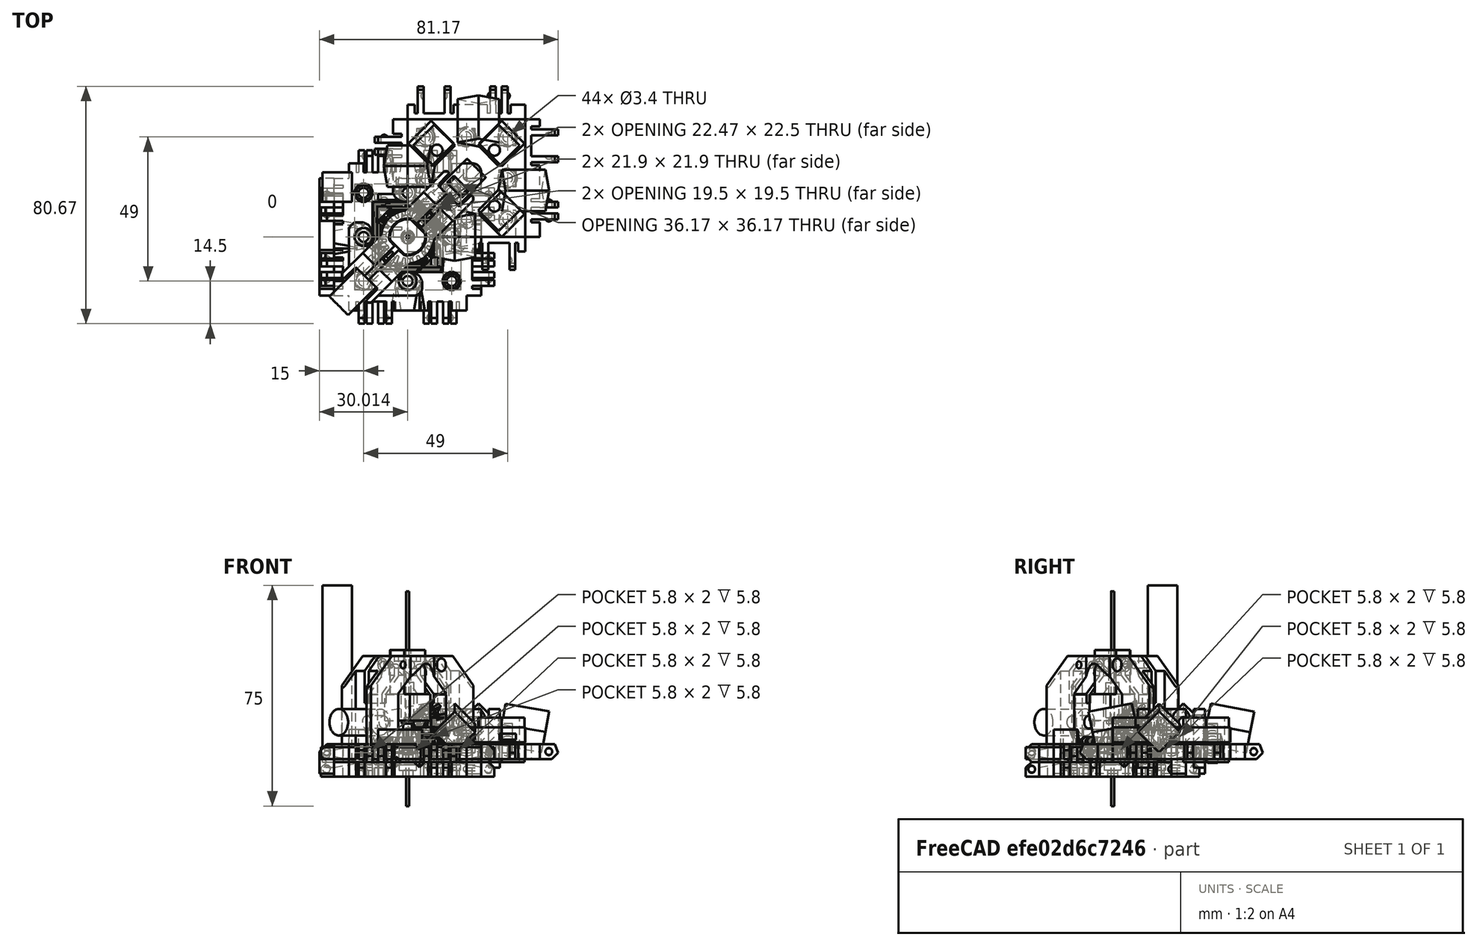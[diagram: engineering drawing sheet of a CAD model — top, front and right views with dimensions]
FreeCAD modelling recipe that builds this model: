
FCSTD DOCUMENT  (FreeCAD 0.18R16146 (Git))
Label: Robot 0.2
License: All rights reserved
LicenseURL: http://en.wikipedia.org/wiki/All_rights_reserved
objects: Part::Box×352, Part::Cut×133, Part::Sphere×107, Part::MultiFuse×99, Part::Cylinder×68, Part::Fuse×45, Part::Chamfer×23, Part::Feature×21, Drawing::FeatureViewAnnotation×10, Part::Fillet×7, App::DocumentObjectGroup×4, Part::MultiCommon×4, Drawing::FeaturePage×2, Part::FeaturePython×2, Part::Cone×2, Part::Mirroring×1
note: 864 computed .brp shape members not serialized (recipe doc carries the construction recipe); baked Part::Feature solids carry a one-line shape summary decoded from their .brp

FEATURE [Part::Box] Box  label="Cube"
  AttacherType = Attacher::AttachEngine3D
  Height = 5
  Length = 40
  Placement = pos=(-20,-20,-2) rot=(0,0,1;0rad)
  Width = 40
FEATURE [Part::Sphere] Sphere003  label="Mag Hole 3"
  Angle1 = -90
  Angle2 = 90
  Angle3 = 360
  AttacherType = Attacher::AttachEngine3D
  Placement = pos=(-15,15,1.7) rot=(0,0,1;0rad)
  Radius = 2.83
FEATURE [Part::Sphere] Sphere005  label="Mag Hole 2"
  Angle1 = -90
  Angle2 = 90
  Angle3 = 360
  AttacherType = Attacher::AttachEngine3D
  Placement = pos=(15,0,1.7) rot=(0,0,1;0rad)
  Radius = 2.825
FEATURE [Part::Sphere] Sphere  label="Mag Hole"
  Angle1 = -90
  Angle2 = 90
  Angle3 = 360
  AttacherType = Attacher::AttachEngine3D
  Placement = pos=(-15,-15,1.7) rot=(0,0,1;0rad)
  Radius = 2.83
FEATURE [Part::MultiFuse] Fusion004  label="Ball Holes"
  Shapes = -> [Sphere,Sphere005,Sphere003]
FEATURE [Part::Cut] Cut003
  Base = -> Box
  Tool = -> Fusion004
FEATURE [Part::Box] Box001  label="Cube001"
  AttacherType = Attacher::AttachEngine3D
  Height = 7
  Length = 5
  Placement = pos=(-5,0,-2) rot=(0,0,1;0rad)
  Width = 40
FEATURE [Part::Box] Box002  label="Cube002"
  AttacherType = Attacher::AttachEngine3D
  Height = 7
  Length = 10
  Placement = pos=(-15,6,-2) rot=(0,0,1;0rad)
  Width = 2
FEATURE [Part::Box] Box003  label="Cube003"
  AttacherType = Attacher::AttachEngine3D
  Height = 7
  Length = 10
  Placement = pos=(-15,10,-2) rot=(0,0,1;0rad)
  Width = 2
FEATURE [Part::Box] Box004  label="Cube004"
  AttacherType = Attacher::AttachEngine3D
  Height = 7
  Length = 10
  Placement = pos=(-15,25.4,-2) rot=(0,0,1;0rad)
  Width = 2
FEATURE [Part::Box] Box005  label="Cube005"
  AttacherType = Attacher::AttachEngine3D
  Height = 7
  Length = 10
  Placement = pos=(-15,34.6,-2) rot=(0,0,1;0rad)
  Width = 2
FEATURE [Part::Sphere] Sphere008
  Angle1 = -90
  Angle2 = 90
  Angle3 = 360
  AttacherType = Attacher::AttachEngine3D
  Placement = pos=(-7.5,6.5,0.5) rot=(0,0,1;0rad)
  Radius = 1.25
FEATURE [Part::Box] Box006  label="Chamfer Cube"
  AttacherType = Attacher::AttachEngine3D
  Height = 10
  Length = 13
  Placement = pos=(-11.69,0,-1.19) rot=(0,-1,0;0.785398rad)
  Width = 40
FEATURE [Part::Sphere] Sphere009
  Angle1 = -90
  Angle2 = 90
  Angle3 = 360
  AttacherType = Attacher::AttachEngine3D
  Placement = pos=(-7.5,11.5,0.5) rot=(0,0,1;0rad)
  Radius = 1.25
FEATURE [Part::Sphere] Sphere010
  Angle1 = -90
  Angle2 = 90
  Angle3 = 360
  AttacherType = Attacher::AttachEngine3D
  Placement = pos=(-7.5,28,0.5) rot=(0,0,1;0rad)
  Radius = 1.5
FEATURE [Part::Sphere] Sphere011
  Angle1 = -90
  Angle2 = 90
  Angle3 = 360
  AttacherType = Attacher::AttachEngine3D
  Placement = pos=(-7.5,34,0.5) rot=(0,0,1;0rad)
  Radius = 1.5
FEATURE [Part::Box] Box007  label="Cube007"
  AttacherType = Attacher::AttachEngine3D
  Height = 7
  Length = 4
  Placement = pos=(-6,5,-2) rot=(0,0,1;0rad)
  Width = 1
FEATURE [Part::Box] Box008  label="Cube008"
  AttacherType = Attacher::AttachEngine3D
  Height = 7
  Length = 4
  Placement = pos=(-6,8,-2) rot=(0,0,1;0rad)
  Width = 2
FEATURE [Part::Box] Box009  label="Cube009"
  AttacherType = Attacher::AttachEngine3D
  Height = 7
  Length = 4
  Placement = pos=(-6,12,-2) rot=(0,0,1;0rad)
  Width = 1
FEATURE [Part::Box] Box010  label="Cube010"
  AttacherType = Attacher::AttachEngine3D
  Height = 7
  Length = 4
  Placement = pos=(-6,24.4,-2) rot=(0,0,1;0rad)
  Width = 1
FEATURE [Part::Box] Box011  label="Cube011"
  AttacherType = Attacher::AttachEngine3D
  Height = 7
  Length = 4
  Placement = pos=(-6,36.6,-2) rot=(0,0,1;0rad)
  Width = 1
FEATURE [Part::Box] Box012  label="Cube012"
  AttacherType = Attacher::AttachEngine3D
  Height = 7
  Length = 4
  Placement = pos=(-6,27.4,-2) rot=(0,0,1;0rad)
  Width = 7.2
FEATURE [Part::MultiFuse] Fusion003  label="Extra Holes for Clips"
  Shapes = -> [Box012,Box009,Box011,Box008,Box010,Box007]
FEATURE [Part::Box] Box013  label="Re-level Edge Clip Block"
  AttacherType = Attacher::AttachEngine3D
  Height = 10
  Length = 20
  Placement = pos=(-19,-2,3) rot=(0,0,1;0rad)
  Width = 44
FEATURE [Part::Box] Box014  label="Cube014"
  AttacherType = Attacher::AttachEngine3D
  Height = 7
  Length = 10
  Placement = pos=(-10,34.6,0) rot=(0,0,1;0rad)
  Width = 2
FEATURE [Part::Box] Box015  label="Cube015"
  AttacherType = Attacher::AttachEngine3D
  Height = 7
  Length = 5
  Width = 40
FEATURE [Part::Box] Box016  label="Cube016"
  AttacherType = Attacher::AttachEngine3D
  Height = 7
  Length = 10
  Placement = pos=(-10,25.4,0) rot=(0,0,1;0rad)
  Width = 2
FEATURE [Part::Box] Box017  label="Cube017"
  AttacherType = Attacher::AttachEngine3D
  Height = 7
  Length = 10
  Placement = pos=(-10,10,0) rot=(0,0,1;0rad)
  Width = 2
FEATURE [Part::Box] Box018  label="Cube018"
  AttacherType = Attacher::AttachEngine3D
  Height = 7
  Length = 10
  Placement = pos=(-10,6,0) rot=(0,0,1;0rad)
  Width = 2
FEATURE [Part::Sphere] Sphere012
  Angle1 = -90
  Angle2 = 90
  Angle3 = 360
  AttacherType = Attacher::AttachEngine3D
  Placement = pos=(-3,6.5,2.5) rot=(0,0,1;0rad)
  Radius = 1.25
FEATURE [Part::Box] Box019  label="Cube019"
  AttacherType = Attacher::AttachEngine3D
  Height = 10
  Length = 13
  Placement = pos=(-10.19,0,-1.19) rot=(0,-1,0;0.785398rad)
  Width = 40
FEATURE [Part::Sphere] Sphere013
  Angle1 = -90
  Angle2 = 90
  Angle3 = 360
  AttacherType = Attacher::AttachEngine3D
  Placement = pos=(-3,11.5,2.5) rot=(0,0,1;0rad)
  Radius = 1.25
FEATURE [Part::Sphere] Sphere014
  Angle1 = -90
  Angle2 = 90
  Angle3 = 360
  AttacherType = Attacher::AttachEngine3D
  Placement = pos=(-3,28,2.5) rot=(0,0,1;0rad)
  Radius = 1.5
FEATURE [Part::Sphere] Sphere015
  Angle1 = -90
  Angle2 = 90
  Angle3 = 360
  AttacherType = Attacher::AttachEngine3D
  Placement = pos=(-3,34,2.5) rot=(0,0,1;0rad)
  Radius = 1.5
FEATURE [Part::MultiFuse] Fusion005
  Shapes = -> [Box015,Box018,Box017,Box016,Box014]
FEATURE [Part::Cut] Cut005
  Base = -> Fusion005
  Tool = -> Box019
FEATURE [Part::MultiFuse] Fusion006
  Shapes = -> [Sphere012,Sphere013,Cut005]
FEATURE [Part::MultiFuse] Fusion007
  Shapes = -> [Sphere015,Sphere014]
FEATURE [Part::Cut] Cut006
  Base = -> Fusion006
  Tool = -> Fusion007
FEATURE [Part::Chamfer] Chamfer002
  Base = -> Cut006
  Edges = 4 edges r=4: [Edge31,Edge37,Edge43,Edge46]
FEATURE [Part::Box] Box020  label="Cube020"
  AttacherType = Attacher::AttachEngine3D
  Height = 7
  Length = 4
  Placement = pos=(-1,5,0) rot=(0,0,1;0rad)
  Width = 1
FEATURE [Part::Box] Box021  label="Cube021"
  AttacherType = Attacher::AttachEngine3D
  Height = 7
  Length = 4
  Placement = pos=(-1,8,0) rot=(0,0,1;0rad)
  Width = 2
FEATURE [Part::Box] Box022  label="Cube022"
  AttacherType = Attacher::AttachEngine3D
  Height = 7
  Length = 4
  Placement = pos=(-1,12,0) rot=(0,0,1;0rad)
  Width = 1
FEATURE [Part::Box] Box023  label="Cube023"
  AttacherType = Attacher::AttachEngine3D
  Height = 7
  Length = 4
  Placement = pos=(-1,24.4,0) rot=(0,0,1;0rad)
  Width = 1
FEATURE [Part::Box] Box024  label="Cube024"
  AttacherType = Attacher::AttachEngine3D
  Height = 7
  Length = 4
  Placement = pos=(-1,36.6,0) rot=(0,0,1;0rad)
  Width = 1
FEATURE [Part::Box] Box025  label="Cube025"
  AttacherType = Attacher::AttachEngine3D
  Height = 7
  Length = 4
  Placement = pos=(-1,27.4,0) rot=(0,0,1;0rad)
  Width = 7.2
FEATURE [Part::MultiFuse] Fusion008
  Shapes = -> [Box025,Box022,Box024,Box021,Box023,Box020]
FEATURE [Part::Cut] Cut007
  Base = -> Chamfer002
  Placement = pos=(-5,40,3) rot=(1,0,0;3.14159rad)
  Tool = -> Fusion008
FEATURE [Part::Box] Box026  label="Cube026"
  AttacherType = Attacher::AttachEngine3D
  Height = 10
  Length = 12
  Placement = pos=(-11,-2,-12) rot=(0,0,1;0rad)
  Width = 44
FEATURE [Part::Cut] Cut008
  Base = -> Cut007
  Placement = pos=(40,0,0) rot=(0,0,1;1.5708rad)
  Tool = -> Box026
FEATURE [Part::Box] Box027  label="Cube027"
  AttacherType = Attacher::AttachEngine3D
  Height = 7
  Length = 4
  Placement = pos=(-1,12,0) rot=(0,0,1;0rad)
  Width = 1
FEATURE [Part::Box] Box028  label="Cube028"
  AttacherType = Attacher::AttachEngine3D
  Height = 10
  Length = 13
  Placement = pos=(-10.19,0,-1.19) rot=(0,-1,0;0.785398rad)
  Width = 40
FEATURE [Part::Box] Box029  label="Cube029"
  AttacherType = Attacher::AttachEngine3D
  Height = 7
  Length = 4
  Placement = pos=(-1,27.4,0) rot=(0,0,1;0rad)
  Width = 7.2
FEATURE [Part::Box] Box030  label="Cube030"
  AttacherType = Attacher::AttachEngine3D
  Height = 7
  Length = 4
  Placement = pos=(-1,5,0) rot=(0,0,1;0rad)
  Width = 1
FEATURE [Part::Box] Box031  label="Cube031"
  AttacherType = Attacher::AttachEngine3D
  Height = 7
  Length = 10
  Placement = pos=(-10,6,0) rot=(0,0,1;0rad)
  Width = 2
FEATURE [Part::Box] Box032  label="Cube032"
  AttacherType = Attacher::AttachEngine3D
  Height = 10
  Length = 12
  Placement = pos=(-11,-2,-12) rot=(0,0,1;0rad)
  Width = 44
FEATURE [Part::Sphere] Sphere016
  Angle1 = -90
  Angle2 = 90
  Angle3 = 360
  AttacherType = Attacher::AttachEngine3D
  Placement = pos=(-3,6.5,2.5) rot=(0,0,1;0rad)
  Radius = 1.25
FEATURE [Part::Box] Box033  label="Cube033"
  AttacherType = Attacher::AttachEngine3D
  Height = 7
  Length = 10
  Placement = pos=(-10,25.4,0) rot=(0,0,1;0rad)
  Width = 2
FEATURE [Part::Box] Box034  label="Cube034"
  AttacherType = Attacher::AttachEngine3D
  Height = 7
  Length = 10
  Placement = pos=(-10,10,0) rot=(0,0,1;0rad)
  Width = 2
FEATURE [Part::Sphere] Sphere017
  Angle1 = -90
  Angle2 = 90
  Angle3 = 360
  AttacherType = Attacher::AttachEngine3D
  Placement = pos=(-3,28,2.5) rot=(0,0,1;0rad)
  Radius = 1.5
FEATURE [Part::Sphere] Sphere018
  Angle1 = -90
  Angle2 = 90
  Angle3 = 360
  AttacherType = Attacher::AttachEngine3D
  Placement = pos=(-3,11.5,2.5) rot=(0,0,1;0rad)
  Radius = 1.25
FEATURE [Part::Box] Box035  label="Cube035"
  AttacherType = Attacher::AttachEngine3D
  Height = 7
  Length = 4
  Placement = pos=(-1,36.6,0) rot=(0,0,1;0rad)
  Width = 1
FEATURE [Part::Sphere] Sphere019
  Angle1 = -90
  Angle2 = 90
  Angle3 = 360
  AttacherType = Attacher::AttachEngine3D
  Placement = pos=(-3,34,2.5) rot=(0,0,1;0rad)
  Radius = 1.5
FEATURE [Part::MultiFuse] Fusion011
  Shapes = -> [Sphere019,Sphere017]
FEATURE [Part::Box] Box036  label="Cube036"
  AttacherType = Attacher::AttachEngine3D
  Height = 7
  Length = 4
  Placement = pos=(-1,8,0) rot=(0,0,1;0rad)
  Width = 2
FEATURE [Part::Box] Box037  label="Cube037"
  AttacherType = Attacher::AttachEngine3D
  Height = 7
  Length = 10
  Placement = pos=(-10,34.6,0) rot=(0,0,1;0rad)
  Width = 2
FEATURE [Part::Box] Box038  label="Cube038"
  AttacherType = Attacher::AttachEngine3D
  Height = 7
  Length = 4
  Placement = pos=(-1,24.4,0) rot=(0,0,1;0rad)
  Width = 1
FEATURE [Part::MultiFuse] Fusion009
  Shapes = -> [Box029,Box027,Box035,Box036,Box038,Box030]
FEATURE [Part::Box] Box039  label="Cube039"
  AttacherType = Attacher::AttachEngine3D
  Height = 7
  Length = 5
  Width = 40
FEATURE [Part::MultiFuse] Fusion012
  Shapes = -> [Box039,Box031,Box034,Box033,Box037]
FEATURE [Part::Cut] Cut011
  Base = -> Fusion012
  Tool = -> Box028
FEATURE [Part::MultiFuse] Fusion010
  Shapes = -> [Sphere016,Sphere018,Cut011]
FEATURE [Part::Cut] Cut012
  Base = -> Fusion010
  Tool = -> Fusion011
FEATURE [Part::Chamfer] Chamfer003
  Base = -> Cut012
  Edges = 4 edges r=4: [Edge31,Edge37,Edge43,Edge46]
FEATURE [Part::Cut] Cut010
  Base = -> Chamfer003
  Placement = pos=(-5,40,3) rot=(1,0,0;3.14159rad)
  Tool = -> Fusion009
FEATURE [Part::Cut] Cut009
  Base = -> Cut010
  Placement = pos=(40,40,0) rot=(0,0,1;3.14159rad)
  Tool = -> Box032
FEATURE [Part::Sphere] Sphere020
  Angle1 = -90
  Angle2 = 90
  Angle3 = 360
  AttacherType = Attacher::AttachEngine3D
  Placement = pos=(-3,11.5,2.5) rot=(0,0,1;0rad)
  Radius = 1.25
FEATURE [Part::Box] Box040  label="Cube040"
  AttacherType = Attacher::AttachEngine3D
  Height = 7
  Length = 10
  Placement = pos=(-10,6,0) rot=(0,0,1;0rad)
  Width = 2
FEATURE [Part::Box] Box041  label="Cube041"
  AttacherType = Attacher::AttachEngine3D
  Height = 7
  Length = 4
  Placement = pos=(-1,8,0) rot=(0,0,1;0rad)
  Width = 2
FEATURE [Part::Box] Box042  label="Cube042"
  AttacherType = Attacher::AttachEngine3D
  Height = 7
  Length = 10
  Placement = pos=(-10,10,0) rot=(0,0,1;0rad)
  Width = 2
FEATURE [Part::Box] Box043  label="Cube043"
  AttacherType = Attacher::AttachEngine3D
  Height = 10
  Length = 12
  Placement = pos=(-11,-2,-12) rot=(0,0,1;0rad)
  Width = 44
FEATURE [Part::Box] Box044  label="Cube044"
  AttacherType = Attacher::AttachEngine3D
  Height = 7
  Length = 4
  Placement = pos=(-1,5,0) rot=(0,0,1;0rad)
  Width = 1
FEATURE [Part::Sphere] Sphere021
  Angle1 = -90
  Angle2 = 90
  Angle3 = 360
  AttacherType = Attacher::AttachEngine3D
  Placement = pos=(-3,28,2.5) rot=(0,0,1;0rad)
  Radius = 1.5
FEATURE [Part::Sphere] Sphere022
  Angle1 = -90
  Angle2 = 90
  Angle3 = 360
  AttacherType = Attacher::AttachEngine3D
  Placement = pos=(-3,6.5,2.5) rot=(0,0,1;0rad)
  Radius = 1.25
FEATURE [Part::Sphere] Sphere023
  Angle1 = -90
  Angle2 = 90
  Angle3 = 360
  AttacherType = Attacher::AttachEngine3D
  Placement = pos=(-3,34,2.5) rot=(0,0,1;0rad)
  Radius = 1.5
FEATURE [Part::Box] Box045  label="Cube045"
  AttacherType = Attacher::AttachEngine3D
  Height = 7
  Length = 4
  Placement = pos=(-1,12,0) rot=(0,0,1;0rad)
  Width = 1
FEATURE [Part::Box] Box046  label="Cube046"
  AttacherType = Attacher::AttachEngine3D
  Height = 7
  Length = 5
  Width = 40
FEATURE [Part::Box] Box047  label="Cube047"
  AttacherType = Attacher::AttachEngine3D
  Height = 7
  Length = 4
  Placement = pos=(-1,36.6,0) rot=(0,0,1;0rad)
  Width = 1
FEATURE [Part::Box] Box048  label="Cube048"
  AttacherType = Attacher::AttachEngine3D
  Height = 7
  Length = 4
  Placement = pos=(-1,24.4,0) rot=(0,0,1;0rad)
  Width = 1
FEATURE [Part::Box] Box049  label="Cube049"
  AttacherType = Attacher::AttachEngine3D
  Height = 7
  Length = 10
  Placement = pos=(-10,25.4,0) rot=(0,0,1;0rad)
  Width = 2
FEATURE [Part::Box] Box050  label="Cube050"
  AttacherType = Attacher::AttachEngine3D
  Height = 10
  Length = 13
  Placement = pos=(-10.19,0,-1.19) rot=(0,-1,0;0.785398rad)
  Width = 40
FEATURE [Part::Box] Box051  label="Cube051"
  AttacherType = Attacher::AttachEngine3D
  Height = 7
  Length = 10
  Placement = pos=(-10,34.6,0) rot=(0,0,1;0rad)
  Width = 2
FEATURE [Part::MultiFuse] Fusion015
  Shapes = -> [Box046,Box040,Box042,Box049,Box051]
FEATURE [Part::Cut] Cut013
  Base = -> Fusion015
  Tool = -> Box050
FEATURE [Part::MultiFuse] Fusion013
  Shapes = -> [Sphere022,Sphere020,Cut013]
FEATURE [Part::MultiFuse] Fusion016
  Shapes = -> [Sphere023,Sphere021]
FEATURE [Part::Cut] Cut014
  Base = -> Fusion013
  Tool = -> Fusion016
FEATURE [Part::Chamfer] Chamfer004
  Base = -> Cut014
  Edges = 4 edges r=4: [Edge31,Edge37,Edge43,Edge46]
FEATURE [Part::Box] Box052  label="Cube052"
  AttacherType = Attacher::AttachEngine3D
  Height = 7
  Length = 4
  Placement = pos=(-1,27.4,0) rot=(0,0,1;0rad)
  Width = 7.2
FEATURE [Part::MultiFuse] Fusion014
  Shapes = -> [Box052,Box045,Box047,Box041,Box048,Box044]
FEATURE [Part::Cut] Cut016
  Base = -> Chamfer004
  Placement = pos=(-5,40,3) rot=(1,0,0;3.14159rad)
  Tool = -> Fusion014
FEATURE [Part::Cut] Cut015
  Base = -> Cut016
  Placement = pos=(0,40,0) rot=(0,0,-1;1.5708rad)
  Tool = -> Box043
FEATURE [Part::Box] Box054  label="Cube054"
  AttacherType = Attacher::AttachEngine3D
  Height = 15
  Length = 10
  Placement = pos=(9,2,-3) rot=(0,0,1;0.785398rad)
  Width = 10
FEATURE [Part::Box] Box055  label="Cube055"
  AttacherType = Attacher::AttachEngine3D
  Height = 15
  Length = 10
  Placement = pos=(31,24,-3) rot=(0,0,1;0.785398rad)
  Width = 10
FEATURE [Part::Box] Box056  label="Cube056"
  AttacherType = Attacher::AttachEngine3D
  Height = 15
  Length = 10
  Placement = pos=(31,2,-3) rot=(0,0,1;0.785398rad)
  Width = 10
FEATURE [Part::Box] Box057  label="Cube057"
  AttacherType = Attacher::AttachEngine3D
  Height = 15
  Length = 10
  Placement = pos=(9,24,-3) rot=(0,0,1;0.785398rad)
  Width = 10
FEATURE [Part::MultiFuse] Fusion017
  Shapes = -> [Box054,Box057,Box056,Box055]
FEATURE [Part::Box] Box058  label="Cube058"
  AttacherType = Attacher::AttachEngine3D
  Height = 5
  Length = 40
  Placement = pos=(0,0,3.7) rot=(0,0,1;0rad)
  Width = 40
FEATURE [Part::Box] Box059  label="Square Nut Hole 008"
  AttacherType = Attacher::AttachEngine3D
  Height = 2
  Length = 5.6
  Placement = pos=(17.2,31.2,4.6) rot=(0,0,1;0rad)
  Width = 5.6
FEATURE [Part::Box] Box060  label="Square Nut Hole 009"
  AttacherType = Attacher::AttachEngine3D
  Height = 2
  Length = 5.6
  Placement = pos=(17.2,-0.85,4.6) rot=(0,0,1;0rad)
  Width = 10
FEATURE [Part::Box] Box061  label="Square Nut Hole 010"
  AttacherType = Attacher::AttachEngine3D
  Height = 2
  Length = 5.6
  Placement = pos=(31.2,-0.85,4.6) rot=(0,0,1;0rad)
  Width = 10
FEATURE [Part::Box] Box062  label="Square Nut Hole 011"
  AttacherType = Attacher::AttachEngine3D
  Height = 2
  Length = 5.4
  Placement = pos=(31.3,17.3,4.6) rot=(0,0,1;0rad)
  Width = 5.4
FEATURE [Part::Box] Box063  label="Square Nut Hole 012"
  AttacherType = Attacher::AttachEngine3D
  Height = 2
  Length = 5.7
  Placement = pos=(3.15,31.15,4.6) rot=(0,0,1;0rad)
  Width = 5.7
FEATURE [Part::Box] Box064  label="Square Nut Hole 013"
  AttacherType = Attacher::AttachEngine3D
  Height = 2
  Length = 5.5
  Placement = pos=(31.25,31.25,4.6) rot=(0,0,1;0rad)
  Width = 5.5
FEATURE [Part::Box] Box065  label="Square Nut Hole 014"
  AttacherType = Attacher::AttachEngine3D
  Height = 2
  Length = 5.8
  Placement = pos=(3.1,17.1,4.6) rot=(0,0,1;0rad)
  Width = 5.8
FEATURE [Part::Box] Box066  label="Square Nut Hole 015"
  AttacherType = Attacher::AttachEngine3D
  Height = 2
  Length = 5.6
  Placement = pos=(3.2,-0.85,4.6) rot=(0,0,1;0rad)
  Width = 10
FEATURE [Part::Sphere] Sphere006  label="Nut Clearence1"
  Angle1 = -90
  Angle2 = 90
  Angle3 = 360
  AttacherType = Attacher::AttachEngine3D
  Placement = pos=(6,6,2.4) rot=(0,0,1;0rad)
  Radius = 3.35
FEATURE [Part::Sphere] Sphere024
  Angle1 = -90
  Angle2 = 90
  Angle3 = 360
  AttacherType = Attacher::AttachEngine3D
  Placement = pos=(6,34,2.4) rot=(0,0,1;0rad)
  Radius = 3.35
FEATURE [Part::Sphere] Sphere007
  Angle1 = -90
  Angle2 = 90
  Angle3 = 360
  AttacherType = Attacher::AttachEngine3D
  Placement = pos=(34,20,2.4) rot=(0,0,1;0rad)
  Radius = 3.35
FEATURE [Part::Sphere] Sphere001
  Angle1 = -90
  Angle2 = 90
  Angle3 = 360
  AttacherType = Attacher::AttachEngine3D
  Placement = pos=(34,6,2.4) rot=(0,0,1;0rad)
  Radius = 3.35
FEATURE [Part::Sphere] Sphere025
  Angle1 = -90
  Angle2 = 90
  Angle3 = 360
  AttacherType = Attacher::AttachEngine3D
  Placement = pos=(20,6,2.4) rot=(0,0,1;0rad)
  Radius = 3.35
FEATURE [Part::Sphere] Sphere026
  Angle1 = -90
  Angle2 = 90
  Angle3 = 360
  AttacherType = Attacher::AttachEngine3D
  Placement = pos=(20,34,2.4) rot=(0,0,1;0rad)
  Radius = 3.35
FEATURE [Part::Sphere] Sphere004
  Angle1 = -90
  Angle2 = 90
  Angle3 = 360
  AttacherType = Attacher::AttachEngine3D
  Placement = pos=(6,20,2.4) rot=(0,0,1;0rad)
  Radius = 3.35
FEATURE [Part::Sphere] Sphere002
  Angle1 = -90
  Angle2 = 90
  Angle3 = 360
  AttacherType = Attacher::AttachEngine3D
  Placement = pos=(34,34,2.4) rot=(0,0,1;0rad)
  Radius = 3.35
FEATURE [Part::Cylinder] Cylinder
  Angle = 360
  AttacherType = Attacher::AttachEngine3D
  Height = 10
  Placement = pos=(6,6,0) rot=(0,0,1;0rad)
  Radius = 1.7
FEATURE [Part::Cylinder] Cylinder002
  Angle = 360
  AttacherType = Attacher::AttachEngine3D
  Height = 10
  Placement = pos=(34,6,0) rot=(0,0,1;0rad)
  Radius = 1.7
FEATURE [Part::Cylinder] Cylinder001
  Angle = 360
  AttacherType = Attacher::AttachEngine3D
  Height = 10
  Placement = pos=(20,6,0) rot=(0,0,1;0rad)
  Radius = 1.7
FEATURE [Part::Cylinder] Cylinder003
  Angle = 360
  AttacherType = Attacher::AttachEngine3D
  Height = 10
  Placement = pos=(34,34,0) rot=(0,0,1;0rad)
  Radius = 1.7
FEATURE [Part::Cylinder] Cylinder004
  Angle = 360
  AttacherType = Attacher::AttachEngine3D
  Height = 10
  Placement = pos=(20,34,0) rot=(0,0,1;0rad)
  Radius = 1.7
FEATURE [Part::Cylinder] Cylinder005
  Angle = 360
  AttacherType = Attacher::AttachEngine3D
  Height = 10
  Placement = pos=(6,34,0) rot=(0,0,1;0rad)
  Radius = 1.7
FEATURE [Part::Cylinder] Cylinder006
  Angle = 360
  AttacherType = Attacher::AttachEngine3D
  Height = 10
  Placement = pos=(6,20,0) rot=(0,0,1;0rad)
  Radius = 1.7
FEATURE [Part::Cylinder] Cylinder007
  Angle = 360
  AttacherType = Attacher::AttachEngine3D
  Height = 10
  Placement = pos=(34,20,0) rot=(0,0,1;0rad)
  Radius = 1.7
FEATURE [Part::MultiFuse] Fusion018
  Shapes = -> [Cylinder,Cylinder004,Cylinder007,Cylinder005,Cylinder006,Cylinder001,Cylinder002,Cylinder003]
FEATURE [Part::MultiFuse] Fusion019
  Shapes = -> [Sphere007,Sphere024,Sphere006,Sphere025,Sphere001,Sphere026,Sphere004,Sphere002]
FEATURE [Part::MultiFuse] Fusion020
  Shapes = -> [Box061,Box065,Box062,Box063,Box064,Box066,Box059,Box060]
FEATURE [Part::Cut] Cut017
  Base = -> Box058
  Tool = -> Fusion020
FEATURE [Part::Cut] Cut019
  Base = -> Cut017
  Tool = -> Fusion019
FEATURE [Part::Cut] Cut018
  Base = -> Cut019
  Tool = -> Fusion018
FEATURE [Part::Cylinder] Cylinder008
  Angle = 360
  AttacherType = Attacher::AttachEngine3D
  Height = 20
  Placement = pos=(10,10.5,-5) rot=(0,0,1;0rad)
  Radius = 1.9
FEATURE [Part::Cylinder] Cylinder009
  Angle = 360
  AttacherType = Attacher::AttachEngine3D
  Height = 20
  Placement = pos=(29.5,10.5,-5) rot=(0,0,1;0rad)
  Radius = 1.9
FEATURE [Part::Cylinder] Cylinder010
  Angle = 360
  AttacherType = Attacher::AttachEngine3D
  Height = 20
  Placement = pos=(29.5,29.5,-5) rot=(0,0,1;0rad)
  Radius = 1.9
FEATURE [Part::Cylinder] Cylinder011
  Angle = 360
  AttacherType = Attacher::AttachEngine3D
  Height = 20
  Placement = pos=(10,29.5,-7) rot=(0,0,1;0rad)
  Radius = 1.9
FEATURE [Part::MultiFuse] Fusion021  label="M2 Screw holes"
  Shapes = -> [Cylinder008,Cylinder009,Cylinder011,Cylinder010]
FEATURE [Part::Box] Box067  label="Square Nut Hole 016"
  AttacherType = Attacher::AttachEngine3D
  Height = 2
  Length = 5.8
  Placement = pos=(31.1,17.1,4.6) rot=(0,0,1;0rad)
  Width = 5.8
FEATURE [Part::Box] Box068  label="Square Nut Hole 017"
  AttacherType = Attacher::AttachEngine3D
  Height = 2
  Length = 5.8
  Placement = pos=(17.1,36.9,2.1) rot=(1,0,0;3.14159rad)
  Width = 5.8
FEATURE [Part::Box] Box069  label="Square Nut Hole 018"
  AttacherType = Attacher::AttachEngine3D
  Height = 2
  Length = 5.8
  Placement = pos=(-2.9,2.9,2.1) rot=(1,0,0;3.14159rad)
  Width = 5.8
FEATURE [Part::Box] Box070  label="Square Nut Hole 019"
  AttacherType = Attacher::AttachEngine3D
  Height = 2
  Length = 5.8
  Placement = pos=(3.1,3.1,4.6) rot=(0,0,1;0rad)
  Width = 5.8
FEATURE [Part::Box] Box071  label="Square Nut Hole 020"
  AttacherType = Attacher::AttachEngine3D
  Height = 2
  Length = 5.8
  Placement = pos=(3.1,31.1,4.6) rot=(0,0,1;0rad)
  Width = 5.8
FEATURE [Part::Box] Box072  label="Square Nut Hole 021"
  AttacherType = Attacher::AttachEngine3D
  Height = 2
  Length = 5.8
  Placement = pos=(17.1,31.1,4.6) rot=(0,0,1;0rad)
  Width = 5.8
FEATURE [Part::Box] Box073  label="Square Nut Hole 022"
  AttacherType = Attacher::AttachEngine3D
  Height = 2
  Length = 5.8
  Placement = pos=(31.1,31.1,4.6) rot=(0,0,1;0rad)
  Width = 5.8
FEATURE [Part::Box] Box074  label="Square Nut Hole 023"
  AttacherType = Attacher::AttachEngine3D
  Height = 2
  Length = 5.8
  Placement = pos=(3.1,17.1,4.6) rot=(0,0,1;0rad)
  Width = 5.8
FEATURE [Part::Cylinder] Cylinder012
  Angle = 360
  AttacherType = Attacher::AttachEngine3D
  Height = 10
  Placement = pos=(6,6,0) rot=(0,0,1;0rad)
  Radius = 1.7
FEATURE [Part::Cylinder] Cylinder013
  Angle = 360
  AttacherType = Attacher::AttachEngine3D
  Height = 10
  Placement = pos=(34,34,0) rot=(0,0,1;0rad)
  Radius = 1.7
FEATURE [Part::Cylinder] Cylinder014
  Angle = 360
  AttacherType = Attacher::AttachEngine3D
  Height = 10
  Placement = pos=(20,34,0) rot=(0,0,1;0rad)
  Radius = 1.7
FEATURE [Part::Cylinder] Cylinder015
  Angle = 360
  AttacherType = Attacher::AttachEngine3D
  Height = 10
  Placement = pos=(6,34,0) rot=(0,0,1;0rad)
  Radius = 1.7
FEATURE [Part::Cylinder] Cylinder016
  Angle = 360
  AttacherType = Attacher::AttachEngine3D
  Height = 10
  Placement = pos=(6,20,0) rot=(0,0,1;0rad)
  Radius = 1.7
FEATURE [Part::Cylinder] Cylinder017
  Angle = 360
  AttacherType = Attacher::AttachEngine3D
  Height = 10
  Placement = pos=(34,20,0) rot=(0,0,1;0rad)
  Radius = 1.7
FEATURE [Part::Cylinder] Cylinder018
  Angle = 360
  AttacherType = Attacher::AttachEngine3D
  Height = 10
  Placement = pos=(0,0,6.7) rot=(1,0,0;3.14159rad)
  Radius = 1.7
FEATURE [Part::Cylinder] Cylinder019
  Angle = 360
  AttacherType = Attacher::AttachEngine3D
  Height = 10
  Placement = pos=(20,34,6.7) rot=(1,0,0;3.14159rad)
  Radius = 1.7
FEATURE [Part::Box] Box075  label="Cube059"
  AttacherType = Attacher::AttachEngine3D
  Height = 5
  Length = 40
  Placement = pos=(-20,-20,-2) rot=(0,0,1;0rad)
  Width = 40
FEATURE [Part::Sphere] Sphere027
  Angle1 = -90
  Angle2 = 90
  Angle3 = 360
  AttacherType = Attacher::AttachEngine3D
  Placement = pos=(34,20,2.4) rot=(0,0,1;0rad)
  Radius = 3.35
FEATURE [Part::Sphere] Sphere028  label="Nut Clearence002"
  Angle1 = -90
  Angle2 = 90
  Angle3 = 360
  AttacherType = Attacher::AttachEngine3D
  Placement = pos=(6,6,2.4) rot=(0,0,1;0rad)
  Radius = 3.35
FEATURE [Part::Sphere] Sphere029
  Angle1 = -90
  Angle2 = 90
  Angle3 = 360
  AttacherType = Attacher::AttachEngine3D
  Placement = pos=(34,34,2.4) rot=(0,0,1;0rad)
  Radius = 3.35
FEATURE [Part::Sphere] Sphere030
  Angle1 = -90
  Angle2 = 90
  Angle3 = 360
  AttacherType = Attacher::AttachEngine3D
  Placement = pos=(0,0,4.3) rot=(1,0,0;3.14159rad)
  Radius = 3.35
FEATURE [Part::Sphere] Sphere031
  Angle1 = -90
  Angle2 = 90
  Angle3 = 360
  AttacherType = Attacher::AttachEngine3D
  Placement = pos=(20,34,4.3) rot=(1,0,0;3.14159rad)
  Radius = 3.35
FEATURE [Part::Sphere] Sphere032
  Angle1 = -90
  Angle2 = 90
  Angle3 = 360
  AttacherType = Attacher::AttachEngine3D
  Placement = pos=(6,34,2.4) rot=(0,0,1;0rad)
  Radius = 3.35
FEATURE [Part::Sphere] Sphere033
  Angle1 = -90
  Angle2 = 90
  Angle3 = 360
  AttacherType = Attacher::AttachEngine3D
  Placement = pos=(6,20,2.4) rot=(0,0,1;0rad)
  Radius = 3.35
FEATURE [Part::Sphere] Sphere034
  Angle1 = -90
  Angle2 = 90
  Angle3 = 360
  AttacherType = Attacher::AttachEngine3D
  Placement = pos=(20,34,2.4) rot=(0,0,1;0rad)
  Radius = 3.35
FEATURE [Part::Box] Box076  label="Cube060"
  AttacherType = Attacher::AttachEngine3D
  Height = 15
  Length = 19.5
  Placement = pos=(-9.75,-9.75,-3) rot=(0,0,1;0rad)
  Width = 19.5
FEATURE [Part::Box] Box077  label="Cube061"
  AttacherType = Attacher::AttachEngine3D
  Height = 15
  Length = 11
  Placement = pos=(8,24,-3) rot=(0,0,1;0.785398rad)
  Width = 11
FEATURE [Part::Box] Box078  label="Cube062"
  AttacherType = Attacher::AttachEngine3D
  Height = 15
  Length = 11
  Placement = pos=(8,0,-3) rot=(0,0,1;0.785398rad)
  Width = 11
FEATURE [Part::Box] Box079  label="Cube063"
  AttacherType = Attacher::AttachEngine3D
  Height = 15
  Length = 11
  Placement = pos=(32,0,-3) rot=(0,0,1;0.785398rad)
  Width = 11
FEATURE [Part::Box] Box080  label="Cube064"
  AttacherType = Attacher::AttachEngine3D
  Height = 15
  Length = 11
  Placement = pos=(32,24,-3) rot=(0,0,1;0.785398rad)
  Width = 11
FEATURE [Part::MultiFuse] Fusion022
  Shapes = -> [Box078,Box077,Box079,Box080]
FEATURE [Part::Cylinder] Cylinder020
  Angle = 360
  AttacherType = Attacher::AttachEngine3D
  Height = 20
  Placement = pos=(29.5,10.5,-5) rot=(0,0,1;0rad)
  Radius = 1.9
FEATURE [Part::Cylinder] Cylinder021
  Angle = 360
  AttacherType = Attacher::AttachEngine3D
  Height = 20
  Placement = pos=(10,29.5,-7) rot=(0,0,1;0rad)
  Radius = 1.9
FEATURE [Part::Cylinder] Cylinder022
  Angle = 360
  AttacherType = Attacher::AttachEngine3D
  Height = 20
  Placement = pos=(10,10.5,-5) rot=(0,0,1;0rad)
  Radius = 1.9
FEATURE [Part::Cylinder] Cylinder023
  Angle = 360
  AttacherType = Attacher::AttachEngine3D
  Height = 20
  Placement = pos=(29.5,29.5,-5) rot=(0,0,1;0rad)
  Radius = 1.9
FEATURE [Part::MultiFuse] Fusion023  label="M2 Screw holes001"
  Shapes = -> [Cylinder022,Cylinder020,Cylinder021,Cylinder023]
FEATURE [App::DocumentObjectGroup] Group  label="Cubes"
  Group = -> [Fusion017,Fusion022]
FEATURE [Part::Box] Box083  label="Cube067"
  AttacherType = Attacher::AttachEngine3D
  Height = 10
  Length = 24
  Placement = pos=(-12,-12,2.1) rot=(0,0,1;0rad)
  Width = 24
FEATURE [Part::Box] Box084  label="Cube068"
  AttacherType = Attacher::AttachEngine3D
  Height = 14
  Length = 20
  Placement = pos=(-10,-10,0) rot=(0,0,1;0rad)
  Width = 20
FEATURE [Part::Cut] Cut020
  Base = -> Box083
  Tool = -> Box084
FEATURE [Part::Chamfer] Chamfer007  label="Glue Channel Ball"
  Base = -> Cut020
  Edges = 8 edges r=0.95: [Edge4,Edge5,Edge14,Edge16,Edge17,Edge18,Edge19,Edge20]
FEATURE [Part::Chamfer] Chamfer008  label="Octogon Ball"
  Base = -> Box076
  Edges = 4 edges r=4: [Edge1,Edge3,Edge5,Edge7]
FEATURE [Part::Box] Box085  label="Cube069"
  AttacherType = Attacher::AttachEngine3D
  Height = 15
  Length = 19.5
  Placement = pos=(-9.75,-9.75,-14) rot=(0,0,1;0rad)
  Width = 19.5
FEATURE [Part::Box] Box086  label="Cube070"
  AttacherType = Attacher::AttachEngine3D
  Height = 10
  Length = 10
  Placement = pos=(4,-26,1) rot=(0.205904,-0.974848,-0.085288;0.803573rad)
  Width = 15
FEATURE [Part::Box] Box089  label="Cube073"
  AttacherType = Attacher::AttachEngine3D
  Height = 10
  Length = 10
  Placement = pos=(17,32.0919,9.95) rot=(-0.225436,0.969773,-0.093378;0.807337rad)
  Width = 15
FEATURE [Part::Box] Box090  label="Cube074"
  AttacherType = Attacher::AttachEngine3D
  Height = 10
  Length = 15
  Placement = pos=(30.8481,15.8,2.86019) rot=(0.974848,0.205904,-0.085288;0.803573rad)
  Width = 10
FEATURE [Part::Box] Box091  label="Cube075"
  AttacherType = Attacher::AttachEngine3D
  Height = 10
  Length = 10
  Placement = pos=(7.9081,17,9.95) rot=(-0.450607,0.280623,0.847469;1.65638rad)
  Width = 15
FEATURE [Part::Box] Box092  label="Cube076"
  AttacherType = Attacher::AttachEngine3D
  Height = 10
  Length = 10
  Placement = pos=(23,7.9081,9.95) rot=(-0.381178,-0.08861,0.920245;3.06822rad)
  Width = 15
FEATURE [Part::Box] Box093  label="Cube077"
  AttacherType = Attacher::AttachEngine3D
  Height = 7
  Length = 5
  Width = 40
FEATURE [Part::Box] Box094  label="Cube078"
  AttacherType = Attacher::AttachEngine3D
  Height = 7
  Length = 10
  Placement = pos=(-10,6,0) rot=(0,0,1;0rad)
  Width = 2
FEATURE [Part::Box] Box095  label="Cube079"
  AttacherType = Attacher::AttachEngine3D
  Height = 7
  Length = 10
  Placement = pos=(-10,10,0) rot=(0,0,1;0rad)
  Width = 2
FEATURE [Part::Box] Box096  label="Cube080"
  AttacherType = Attacher::AttachEngine3D
  Height = 7
  Length = 10
  Placement = pos=(-10,25.4,0) rot=(0,0,1;0rad)
  Width = 2
FEATURE [Part::Box] Box097  label="Cube081"
  AttacherType = Attacher::AttachEngine3D
  Height = 7
  Length = 10
  Placement = pos=(-10,34.6,0) rot=(0,0,1;0rad)
  Width = 2
FEATURE [Part::Sphere] Sphere035
  Angle1 = -90
  Angle2 = 90
  Angle3 = 360
  AttacherType = Attacher::AttachEngine3D
  Placement = pos=(-3,6.5,2.5) rot=(0,0,1;0rad)
  Radius = 1.25
FEATURE [Part::Box] Box098  label="Cube082"
  AttacherType = Attacher::AttachEngine3D
  Height = 10
  Length = 13
  Placement = pos=(-10.19,0,-1.19) rot=(0,-1,0;0.785398rad)
  Width = 40
FEATURE [Part::Sphere] Sphere036
  Angle1 = -90
  Angle2 = 90
  Angle3 = 360
  AttacherType = Attacher::AttachEngine3D
  Placement = pos=(-3,11.5,2.5) rot=(0,0,1;0rad)
  Radius = 1.25
FEATURE [Part::Sphere] Sphere037
  Angle1 = -90
  Angle2 = 90
  Angle3 = 360
  AttacherType = Attacher::AttachEngine3D
  Placement = pos=(-3,28,2.5) rot=(0,0,1;0rad)
  Radius = 1.5
FEATURE [Part::Sphere] Sphere038
  Angle1 = -90
  Angle2 = 90
  Angle3 = 360
  AttacherType = Attacher::AttachEngine3D
  Placement = pos=(-3,34,2.5) rot=(0,0,1;0rad)
  Radius = 1.5
FEATURE [Part::MultiFuse] Fusion030
  Shapes = -> [Box093,Box094,Box095,Box096,Box097]
FEATURE [Part::Cut] Cut025
  Base = -> Fusion030
  Tool = -> Box098
FEATURE [Part::MultiFuse] Fusion031
  Shapes = -> [Sphere035,Sphere036,Cut025]
FEATURE [Part::MultiFuse] Fusion032
  Shapes = -> [Sphere038,Sphere037]
FEATURE [Part::Cut] Cut026
  Base = -> Fusion031
  Tool = -> Fusion032
FEATURE [Part::Chamfer] Chamfer009
  Base = -> Cut026
  Edges = 4 edges r=4: [Edge31,Edge37,Edge43,Edge46]
FEATURE [Part::Box] Box099  label="Cube083"
  AttacherType = Attacher::AttachEngine3D
  Height = 7
  Length = 4
  Placement = pos=(-1,5,0) rot=(0,0,1;0rad)
  Width = 1
FEATURE [Part::Box] Box100  label="Cube084"
  AttacherType = Attacher::AttachEngine3D
  Height = 7
  Length = 4
  Placement = pos=(-1,8,0) rot=(0,0,1;0rad)
  Width = 2
FEATURE [Part::Box] Box101  label="Cube085"
  AttacherType = Attacher::AttachEngine3D
  Height = 7
  Length = 4
  Placement = pos=(-1,12,0) rot=(0,0,1;0rad)
  Width = 1
FEATURE [Part::Box] Box102  label="Cube086"
  AttacherType = Attacher::AttachEngine3D
  Height = 7
  Length = 4
  Placement = pos=(-1,24.4,0) rot=(0,0,1;0rad)
  Width = 1
FEATURE [Part::Box] Box103  label="Cube087"
  AttacherType = Attacher::AttachEngine3D
  Height = 7
  Length = 4
  Placement = pos=(-1,36.6,0) rot=(0,0,1;0rad)
  Width = 1
FEATURE [Part::Box] Box104  label="Cube088"
  AttacherType = Attacher::AttachEngine3D
  Height = 7
  Length = 4
  Placement = pos=(-1,27.4,0) rot=(0,0,1;0rad)
  Width = 7.2
FEATURE [Part::MultiFuse] Fusion033
  Shapes = -> [Box104,Box101,Box103,Box100,Box102,Box099]
FEATURE [Part::Cut] Cut027
  Base = -> Chamfer009
  Placement = pos=(-5,40,3) rot=(1,0,0;3.14159rad)
  Tool = -> Fusion033
FEATURE [Part::Box] Box105  label="Cube089"
  AttacherType = Attacher::AttachEngine3D
  Height = 10
  Length = 12
  Placement = pos=(-11,-2,-12) rot=(0,0,1;0rad)
  Width = 44
FEATURE [Part::Cut] Cut028
  Base = -> Cut027
  Tool = -> Box105
FEATURE [Part::Box] Box106  label="Cube090"
  AttacherType = Attacher::AttachEngine3D
  Height = 7
  Length = 10
  Placement = pos=(-10,34.6,0) rot=(0,0,1;0rad)
  Width = 2
FEATURE [Part::Box] Box107  label="Cube091"
  AttacherType = Attacher::AttachEngine3D
  Height = 7
  Length = 5
  Width = 40
FEATURE [Part::Box] Box108  label="Cube092"
  AttacherType = Attacher::AttachEngine3D
  Height = 7
  Length = 10
  Placement = pos=(-10,25.4,0) rot=(0,0,1;0rad)
  Width = 2
FEATURE [Part::Box] Box109  label="Cube093"
  AttacherType = Attacher::AttachEngine3D
  Height = 7
  Length = 10
  Placement = pos=(-10,10,0) rot=(0,0,1;0rad)
  Width = 2
FEATURE [Part::Box] Box110  label="Cube094"
  AttacherType = Attacher::AttachEngine3D
  Height = 7
  Length = 10
  Placement = pos=(-10,6,0) rot=(0,0,1;0rad)
  Width = 2
FEATURE [Part::Sphere] Sphere039
  Angle1 = -90
  Angle2 = 90
  Angle3 = 360
  AttacherType = Attacher::AttachEngine3D
  Placement = pos=(-3,6.5,2.5) rot=(0,0,1;0rad)
  Radius = 1.25
FEATURE [Part::Box] Box111  label="Cube095"
  AttacherType = Attacher::AttachEngine3D
  Height = 10
  Length = 13
  Placement = pos=(-10.19,0,-1.19) rot=(0,-1,0;0.785398rad)
  Width = 40
FEATURE [Part::Sphere] Sphere040
  Angle1 = -90
  Angle2 = 90
  Angle3 = 360
  AttacherType = Attacher::AttachEngine3D
  Placement = pos=(-3,11.5,2.5) rot=(0,0,1;0rad)
  Radius = 1.25
FEATURE [Part::Sphere] Sphere041
  Angle1 = -90
  Angle2 = 90
  Angle3 = 360
  AttacherType = Attacher::AttachEngine3D
  Placement = pos=(-3,28,2.5) rot=(0,0,1;0rad)
  Radius = 1.5
FEATURE [Part::Sphere] Sphere042
  Angle1 = -90
  Angle2 = 90
  Angle3 = 360
  AttacherType = Attacher::AttachEngine3D
  Placement = pos=(-3,34,2.5) rot=(0,0,1;0rad)
  Radius = 1.5
FEATURE [Part::MultiFuse] Fusion034
  Shapes = -> [Box107,Box110,Box109,Box108,Box106]
FEATURE [Part::Cut] Cut029
  Base = -> Fusion034
  Tool = -> Box111
FEATURE [Part::MultiFuse] Fusion035
  Shapes = -> [Sphere039,Sphere040,Cut029]
FEATURE [Part::MultiFuse] Fusion036
  Shapes = -> [Sphere042,Sphere041]
FEATURE [Part::Cut] Cut030
  Base = -> Fusion035
  Tool = -> Fusion036
FEATURE [Part::Chamfer] Chamfer010
  Base = -> Cut030
  Edges = 4 edges r=4: [Edge31,Edge37,Edge43,Edge46]
FEATURE [Part::Box] Box112  label="Cube096"
  AttacherType = Attacher::AttachEngine3D
  Height = 7
  Length = 4
  Placement = pos=(-1,5,0) rot=(0,0,1;0rad)
  Width = 1
FEATURE [Part::Box] Box113  label="Cube097"
  AttacherType = Attacher::AttachEngine3D
  Height = 7
  Length = 4
  Placement = pos=(-1,8,0) rot=(0,0,1;0rad)
  Width = 2
FEATURE [Part::Box] Box114  label="Cube098"
  AttacherType = Attacher::AttachEngine3D
  Height = 7
  Length = 4
  Placement = pos=(-1,12,0) rot=(0,0,1;0rad)
  Width = 1
FEATURE [Part::Box] Box115  label="Cube099"
  AttacherType = Attacher::AttachEngine3D
  Height = 7
  Length = 4
  Placement = pos=(-1,24.4,0) rot=(0,0,1;0rad)
  Width = 1
FEATURE [Part::Box] Box116  label="Cube100"
  AttacherType = Attacher::AttachEngine3D
  Height = 7
  Length = 4
  Placement = pos=(-1,36.6,0) rot=(0,0,1;0rad)
  Width = 1
FEATURE [Part::Box] Box117  label="Cube101"
  AttacherType = Attacher::AttachEngine3D
  Height = 7
  Length = 4
  Placement = pos=(-1,27.4,0) rot=(0,0,1;0rad)
  Width = 7.2
FEATURE [Part::MultiFuse] Fusion037
  Shapes = -> [Box117,Box114,Box116,Box113,Box115,Box112]
FEATURE [Part::Cut] Cut031
  Base = -> Chamfer010
  Placement = pos=(-5,40,3) rot=(1,0,0;3.14159rad)
  Tool = -> Fusion037
FEATURE [Part::Box] Box118  label="Cube102"
  AttacherType = Attacher::AttachEngine3D
  Height = 10
  Length = 12
  Placement = pos=(-11,-2,-12) rot=(0,0,1;0rad)
  Width = 44
FEATURE [Part::Cut] Cut032
  Base = -> Cut031
  Placement = pos=(40,0,0) rot=(0,0,1;1.5708rad)
  Tool = -> Box118
FEATURE [Part::Box] Box119  label="Cube103"
  AttacherType = Attacher::AttachEngine3D
  Height = 7
  Length = 4
  Placement = pos=(-1,12,0) rot=(0,0,1;0rad)
  Width = 1
FEATURE [Part::Box] Box120  label="Cube104"
  AttacherType = Attacher::AttachEngine3D
  Height = 10
  Length = 13
  Placement = pos=(-10.19,0,-1.19) rot=(0,-1,0;0.785398rad)
  Width = 40
FEATURE [Part::Box] Box121  label="Cube105"
  AttacherType = Attacher::AttachEngine3D
  Height = 7
  Length = 4
  Placement = pos=(-1,27.4,0) rot=(0,0,1;0rad)
  Width = 7.2
FEATURE [Part::Box] Box122  label="Cube106"
  AttacherType = Attacher::AttachEngine3D
  Height = 7
  Length = 4
  Placement = pos=(-1,5,0) rot=(0,0,1;0rad)
  Width = 1
FEATURE [Part::Box] Box123  label="Cube107"
  AttacherType = Attacher::AttachEngine3D
  Height = 7
  Length = 10
  Placement = pos=(-10,6,0) rot=(0,0,1;0rad)
  Width = 2
FEATURE [Part::Box] Box124  label="Cube108"
  AttacherType = Attacher::AttachEngine3D
  Height = 10
  Length = 12
  Placement = pos=(-11,-2,-12) rot=(0,0,1;0rad)
  Width = 44
FEATURE [Part::Sphere] Sphere043
  Angle1 = -90
  Angle2 = 90
  Angle3 = 360
  AttacherType = Attacher::AttachEngine3D
  Placement = pos=(-3,6.5,2.5) rot=(0,0,1;0rad)
  Radius = 1.25
FEATURE [Part::Box] Box125  label="Cube109"
  AttacherType = Attacher::AttachEngine3D
  Height = 7
  Length = 10
  Placement = pos=(-10,25.4,0) rot=(0,0,1;0rad)
  Width = 2
FEATURE [Part::Box] Box126  label="Cube110"
  AttacherType = Attacher::AttachEngine3D
  Height = 7
  Length = 10
  Placement = pos=(-10,10,0) rot=(0,0,1;0rad)
  Width = 2
FEATURE [Part::Sphere] Sphere044
  Angle1 = -90
  Angle2 = 90
  Angle3 = 360
  AttacherType = Attacher::AttachEngine3D
  Placement = pos=(-3,28,2.5) rot=(0,0,1;0rad)
  Radius = 1.5
FEATURE [Part::Sphere] Sphere045
  Angle1 = -90
  Angle2 = 90
  Angle3 = 360
  AttacherType = Attacher::AttachEngine3D
  Placement = pos=(-3,11.5,2.5) rot=(0,0,1;0rad)
  Radius = 1.25
FEATURE [Part::Box] Box127  label="Cube111"
  AttacherType = Attacher::AttachEngine3D
  Height = 7
  Length = 4
  Placement = pos=(-1,36.6,0) rot=(0,0,1;0rad)
  Width = 1
FEATURE [Part::Sphere] Sphere046
  Angle1 = -90
  Angle2 = 90
  Angle3 = 360
  AttacherType = Attacher::AttachEngine3D
  Placement = pos=(-3,34,2.5) rot=(0,0,1;0rad)
  Radius = 1.5
FEATURE [Part::MultiFuse] Fusion040
  Shapes = -> [Sphere046,Sphere044]
FEATURE [Part::Box] Box128  label="Cube112"
  AttacherType = Attacher::AttachEngine3D
  Height = 7
  Length = 4
  Placement = pos=(-1,8,0) rot=(0,0,1;0rad)
  Width = 2
FEATURE [Part::Box] Box129  label="Cube113"
  AttacherType = Attacher::AttachEngine3D
  Height = 7
  Length = 10
  Placement = pos=(-10,34.6,0) rot=(0,0,1;0rad)
  Width = 2
FEATURE [Part::Box] Box130  label="Cube114"
  AttacherType = Attacher::AttachEngine3D
  Height = 7
  Length = 4
  Placement = pos=(-1,24.4,0) rot=(0,0,1;0rad)
  Width = 1
FEATURE [Part::MultiFuse] Fusion038
  Shapes = -> [Box121,Box119,Box127,Box128,Box130,Box122]
FEATURE [Part::Box] Box131  label="Cube115"
  AttacherType = Attacher::AttachEngine3D
  Height = 7
  Length = 5
  Width = 40
FEATURE [Part::MultiFuse] Fusion041
  Shapes = -> [Box131,Box123,Box126,Box125,Box129]
FEATURE [Part::Cut] Cut035
  Base = -> Fusion041
  Tool = -> Box120
FEATURE [Part::MultiFuse] Fusion039
  Shapes = -> [Sphere043,Sphere045,Cut035]
FEATURE [Part::Cut] Cut036
  Base = -> Fusion039
  Tool = -> Fusion040
FEATURE [Part::Chamfer] Chamfer011
  Base = -> Cut036
  Edges = 4 edges r=4: [Edge31,Edge37,Edge43,Edge46]
FEATURE [Part::Cut] Cut034
  Base = -> Chamfer011
  Placement = pos=(-5,40,3) rot=(1,0,0;3.14159rad)
  Tool = -> Fusion038
FEATURE [Part::Cut] Cut033
  Base = -> Cut034
  Placement = pos=(40,40,0) rot=(0,0,1;3.14159rad)
  Tool = -> Box124
FEATURE [Part::Sphere] Sphere047
  Angle1 = -90
  Angle2 = 90
  Angle3 = 360
  AttacherType = Attacher::AttachEngine3D
  Placement = pos=(-3,11.5,2.5) rot=(0,0,1;0rad)
  Radius = 1.25
FEATURE [Part::Box] Box132  label="Cube116"
  AttacherType = Attacher::AttachEngine3D
  Height = 7
  Length = 10
  Placement = pos=(-10,6,0) rot=(0,0,1;0rad)
  Width = 2
FEATURE [Part::Box] Box133  label="Cube117"
  AttacherType = Attacher::AttachEngine3D
  Height = 7
  Length = 4
  Placement = pos=(-1,8,0) rot=(0,0,1;0rad)
  Width = 2
FEATURE [Part::Box] Box134  label="Cube118"
  AttacherType = Attacher::AttachEngine3D
  Height = 7
  Length = 10
  Placement = pos=(-10,10,0) rot=(0,0,1;0rad)
  Width = 2
FEATURE [Part::Box] Box135  label="Cube119"
  AttacherType = Attacher::AttachEngine3D
  Height = 10
  Length = 12
  Placement = pos=(-11,-2,-12) rot=(0,0,1;0rad)
  Width = 44
FEATURE [Part::Box] Box136  label="Cube120"
  AttacherType = Attacher::AttachEngine3D
  Height = 7
  Length = 4
  Placement = pos=(-1,5,0) rot=(0,0,1;0rad)
  Width = 1
FEATURE [Part::Sphere] Sphere048
  Angle1 = -90
  Angle2 = 90
  Angle3 = 360
  AttacherType = Attacher::AttachEngine3D
  Placement = pos=(-3,28,2.5) rot=(0,0,1;0rad)
  Radius = 1.5
FEATURE [Part::Sphere] Sphere049
  Angle1 = -90
  Angle2 = 90
  Angle3 = 360
  AttacherType = Attacher::AttachEngine3D
  Placement = pos=(-3,6.5,2.5) rot=(0,0,1;0rad)
  Radius = 1.25
FEATURE [Part::Sphere] Sphere050
  Angle1 = -90
  Angle2 = 90
  Angle3 = 360
  AttacherType = Attacher::AttachEngine3D
  Placement = pos=(-3,34,2.5) rot=(0,0,1;0rad)
  Radius = 1.5
FEATURE [Part::Box] Box137  label="Cube121"
  AttacherType = Attacher::AttachEngine3D
  Height = 7
  Length = 4
  Placement = pos=(-1,12,0) rot=(0,0,1;0rad)
  Width = 1
FEATURE [Part::Box] Box138  label="Cube122"
  AttacherType = Attacher::AttachEngine3D
  Height = 7
  Length = 5
  Width = 40
FEATURE [Part::Box] Box139  label="Cube123"
  AttacherType = Attacher::AttachEngine3D
  Height = 7
  Length = 4
  Placement = pos=(-1,36.6,0) rot=(0,0,1;0rad)
  Width = 1
FEATURE [Part::Box] Box140  label="Cube124"
  AttacherType = Attacher::AttachEngine3D
  Height = 7
  Length = 4
  Placement = pos=(-1,24.4,0) rot=(0,0,1;0rad)
  Width = 1
FEATURE [Part::Box] Box141  label="Cube125"
  AttacherType = Attacher::AttachEngine3D
  Height = 7
  Length = 10
  Placement = pos=(-10,25.4,0) rot=(0,0,1;0rad)
  Width = 2
FEATURE [Part::Box] Box142  label="Cube126"
  AttacherType = Attacher::AttachEngine3D
  Height = 10
  Length = 13
  Placement = pos=(-10.19,0,-1.19) rot=(0,-1,0;0.785398rad)
  Width = 40
FEATURE [Part::Box] Box143  label="Cube127"
  AttacherType = Attacher::AttachEngine3D
  Height = 7
  Length = 10
  Placement = pos=(-10,34.6,0) rot=(0,0,1;0rad)
  Width = 2
FEATURE [Part::MultiFuse] Fusion044
  Shapes = -> [Box138,Box132,Box134,Box141,Box143]
FEATURE [Part::Cut] Cut037
  Base = -> Fusion044
  Tool = -> Box142
FEATURE [Part::MultiFuse] Fusion042
  Shapes = -> [Sphere049,Sphere047,Cut037]
FEATURE [Part::MultiFuse] Fusion045
  Shapes = -> [Sphere050,Sphere048]
FEATURE [Part::Cut] Cut038
  Base = -> Fusion042
  Tool = -> Fusion045
FEATURE [Part::Chamfer] Chamfer012
  Base = -> Cut038
  Edges = 4 edges r=4: [Edge31,Edge37,Edge43,Edge46]
FEATURE [Part::Box] Box144  label="Cube128"
  AttacherType = Attacher::AttachEngine3D
  Height = 7
  Length = 4
  Placement = pos=(-1,27.4,0) rot=(0,0,1;0rad)
  Width = 7.2
FEATURE [Part::MultiFuse] Fusion043
  Shapes = -> [Box144,Box137,Box139,Box133,Box140,Box136]
FEATURE [Part::Cut] Cut040
  Base = -> Chamfer012
  Placement = pos=(-5,40,3) rot=(1,0,0;3.14159rad)
  Tool = -> Fusion043
FEATURE [Part::Cut] Cut039
  Base = -> Cut040
  Placement = pos=(0,40,0) rot=(0,0,-1;1.5708rad)
  Tool = -> Box135
FEATURE [Part::MultiFuse] Fusion048
  Shapes = -> [Box089,Box091,Box090,Box092]
FEATURE [Part::Box] Box145  label="Cube129"
  AttacherType = Attacher::AttachEngine3D
  Height = 15
  Length = 19.5
  Placement = pos=(-9.75,-9.75,-14) rot=(0,0,1;0rad)
  Width = 19.5
FEATURE [Part::Box] Box146  label="Cube130"
  AttacherType = Attacher::AttachEngine3D
  Height = 15
  Length = 19.5
  Placement = pos=(-9.75,-9.75,-3) rot=(0,0,1;0rad)
  Width = 19.5
FEATURE [Part::Chamfer] Chamfer013  label="Octagon"
  Base = -> Box146
  Edges = 4 edges r=4: [Edge1,Edge3,Edge5,Edge7]
FEATURE [Part::Box] Box147  label="Cube131"
  AttacherType = Attacher::AttachEngine3D
  Height = 10
  Length = 24
  Placement = pos=(-12,-12,2.1) rot=(0,0,1;0rad)
  Width = 24
FEATURE [Part::Box] Box148  label="Cube132"
  AttacherType = Attacher::AttachEngine3D
  Height = 14
  Length = 20
  Placement = pos=(-10,-10,0) rot=(0,0,1;0rad)
  Width = 20
FEATURE [Part::Cut] Cut043
  Base = -> Box147
  Tool = -> Box148
FEATURE [Part::Chamfer] Chamfer014  label="Glue Channel"
  Base = -> Cut043
  Edges = 8 edges r=0.95: [Edge4,Edge5,Edge14,Edge16,Edge17,Edge18,Edge19,Edge20]
FEATURE [Part::Cut] Cut047
  Base = -> Cut003
  Tool = -> Chamfer007
FEATURE [Part::Cylinder] Cylinder024
  Angle = 360
  AttacherType = Attacher::AttachEngine3D
  Height = 10
  Placement = pos=(-15,-15,-5) rot=(0,0,1;0rad)
  Radius = 1.7
FEATURE [Part::Cylinder] Cylinder025
  Angle = 360
  AttacherType = Attacher::AttachEngine3D
  Height = 10
  Placement = pos=(15,0,-5) rot=(0,0,1;0rad)
  Radius = 1.7
FEATURE [Part::Cylinder] Cylinder026
  Angle = 360
  AttacherType = Attacher::AttachEngine3D
  Height = 10
  Placement = pos=(-15,15,-5) rot=(0,0,1;0rad)
  Radius = 1.7
FEATURE [Part::MultiFuse] Fusion052  label="Screw Holes to remove ball mags"
  Shapes = -> [Cylinder024,Cylinder025,Cylinder026]
FEATURE [Drawing::FeatureViewAnnotation] Annotation
  Font = Sans
  Rotation = 0
  Scale = 7
  Text = 0.4Added in Holes to Mag plate for removal of magnet
  ViewResult = <g transform="translate(14,23) rotate(0)">\n<text id="Annotation"\n font-family="Sans"\n font-size="7"\n fill="#000000">\n<tspan x="0" dy="1em">0.4Added in Holes to Mag plate for removal of magnet</tspan>\n</text>\n</g>
  Visible = false
  X = 14
  Y = 23
FEATURE [Part::Box] Box149  label="Re-level Edge Clip Block001"
  AttacherType = Attacher::AttachEngine3D
  Height = 10
  Length = 12
  Placement = pos=(-21.5,-2,-7) rot=(0,0,1;0rad)
  Width = 44
FEATURE [Part::Fuse] Fusion  label="Bumps"
  Base = -> Sphere008
  Tool = -> Sphere009
FEATURE [Part::Fuse] Fusion053  label="Holes"
  Base = -> Sphere010
  Tool = -> Sphere011
FEATURE [Part::MultiFuse] Fusion054
  Shapes = -> [Box001,Box002,Box003,Box004,Box005]
FEATURE [Part::Fuse] Fusion055
  Base = -> Fusion
  Tool = -> Fusion054
FEATURE [Part::Cut] Cut
  Base = -> Fusion055
  Tool = -> Fusion053
FEATURE [Part::Cut] Cut056
  Base = -> Cut
  Tool = -> Fusion003
FEATURE [Part::Cut] Cut057
  Base = -> Cut056
  Tool = -> Box013
FEATURE [Part::Cut] Cut058
  Base = -> Cut057
  Tool = -> Box149
FEATURE [Part::Cut] Cut059  label="Edge Clips Master"
  Base = -> Cut058
  Placement = pos=(-20,-20,0) rot=(0,0,1;0rad)
  Tool = -> Box006
FEATURE [Part::Box] Box150  label="Cube133"
  AttacherType = Attacher::AttachEngine3D
  Height = 7
  Length = 5
  Placement = pos=(-5,0,-2) rot=(0,0,1;0rad)
  Width = 40
FEATURE [Part::Box] Box151  label="Cube134"
  AttacherType = Attacher::AttachEngine3D
  Height = 7
  Length = 10
  Placement = pos=(-15,6,-2) rot=(0,0,1;0rad)
  Width = 2
FEATURE [Part::Box] Box152  label="Cube135"
  AttacherType = Attacher::AttachEngine3D
  Height = 7
  Length = 10
  Placement = pos=(-15,10,-2) rot=(0,0,1;0rad)
  Width = 2
FEATURE [Part::Box] Box153  label="Cube136"
  AttacherType = Attacher::AttachEngine3D
  Height = 7
  Length = 10
  Placement = pos=(-15,25.4,-2) rot=(0,0,1;0rad)
  Width = 2
FEATURE [Part::Box] Box154  label="Cube137"
  AttacherType = Attacher::AttachEngine3D
  Height = 7
  Length = 10
  Placement = pos=(-15,34.6,-2) rot=(0,0,1;0rad)
  Width = 2
FEATURE [Part::Sphere] Sphere051
  Angle1 = -90
  Angle2 = 90
  Angle3 = 360
  AttacherType = Attacher::AttachEngine3D
  Placement = pos=(-7.5,6.5,0.5) rot=(0,0,1;0rad)
  Radius = 1.25
FEATURE [Part::Box] Box155  label="Chamfer Cube001"
  AttacherType = Attacher::AttachEngine3D
  Height = 10
  Length = 13
  Placement = pos=(-11.69,0,-1.19) rot=(0,-1,0;0.785398rad)
  Width = 40
FEATURE [Part::Sphere] Sphere052
  Angle1 = -90
  Angle2 = 90
  Angle3 = 360
  AttacherType = Attacher::AttachEngine3D
  Placement = pos=(-7.5,11.5,0.5) rot=(0,0,1;0rad)
  Radius = 1.25
FEATURE [Part::Sphere] Sphere053
  Angle1 = -90
  Angle2 = 90
  Angle3 = 360
  AttacherType = Attacher::AttachEngine3D
  Placement = pos=(-7.5,28,0.5) rot=(0,0,1;0rad)
  Radius = 1.5
FEATURE [Part::Sphere] Sphere054
  Angle1 = -90
  Angle2 = 90
  Angle3 = 360
  AttacherType = Attacher::AttachEngine3D
  Placement = pos=(-7.5,34,0.5) rot=(0,0,1;0rad)
  Radius = 1.5
FEATURE [Part::Box] Box156  label="Cube138"
  AttacherType = Attacher::AttachEngine3D
  Height = 7
  Length = 4
  Placement = pos=(-6,5,-2) rot=(0,0,1;0rad)
  Width = 1
FEATURE [Part::Box] Box157  label="Cube139"
  AttacherType = Attacher::AttachEngine3D
  Height = 7
  Length = 4
  Placement = pos=(-6,8,-2) rot=(0,0,1;0rad)
  Width = 2
FEATURE [Part::Box] Box158  label="Cube140"
  AttacherType = Attacher::AttachEngine3D
  Height = 7
  Length = 4
  Placement = pos=(-6,12,-2) rot=(0,0,1;0rad)
  Width = 1
FEATURE [Part::Box] Box159  label="Cube141"
  AttacherType = Attacher::AttachEngine3D
  Height = 7
  Length = 4
  Placement = pos=(-6,24.4,-2) rot=(0,0,1;0rad)
  Width = 1
FEATURE [Part::Box] Box160  label="Cube142"
  AttacherType = Attacher::AttachEngine3D
  Height = 7
  Length = 4
  Placement = pos=(-6,36.6,-2) rot=(0,0,1;0rad)
  Width = 1
FEATURE [Part::Box] Box161  label="Cube143"
  AttacherType = Attacher::AttachEngine3D
  Height = 7
  Length = 4
  Placement = pos=(-6,27.4,-2) rot=(0,0,1;0rad)
  Width = 7.2
FEATURE [Part::MultiFuse] Fusion056  label="Extra Holes for Clips001"
  Shapes = -> [Box161,Box158,Box160,Box157,Box159,Box156]
FEATURE [Part::Box] Box162  label="Re-level Edge Clip Block002"
  AttacherType = Attacher::AttachEngine3D
  Height = 10
  Length = 20
  Placement = pos=(-19,-2,3) rot=(0,0,1;0rad)
  Width = 44
FEATURE [Part::Box] Box163  label="Re-level Edge Clip Block003"
  AttacherType = Attacher::AttachEngine3D
  Height = 10
  Length = 12
  Placement = pos=(-21.5,-2,-7) rot=(0,0,1;0rad)
  Width = 44
FEATURE [Part::Fuse] Fusion057  label="Bumps001"
  Base = -> Sphere051
  Tool = -> Sphere052
FEATURE [Part::Fuse] Fusion058  label="Holes001"
  Base = -> Sphere053
  Tool = -> Sphere054
FEATURE [Part::MultiFuse] Fusion059
  Shapes = -> [Box150,Box151,Box152,Box153,Box154]
FEATURE [Part::Fuse] Fusion060
  Base = -> Fusion057
  Tool = -> Fusion059
FEATURE [Part::Cut] Cut060
  Base = -> Fusion060
  Tool = -> Fusion058
FEATURE [Part::Cut] Cut061
  Base = -> Cut060
  Tool = -> Fusion056
FEATURE [Part::Cut] Cut062
  Base = -> Cut061
  Tool = -> Box162
FEATURE [Part::Cut] Cut063
  Base = -> Cut062
  Tool = -> Box163
FEATURE [Part::Cut] Cut064  label="Copy Edge Clip"
  Base = -> Cut063
  Placement = pos=(-27,20,-7) rot=(0.707107,0,-0.707107;3.14159rad)
  Tool = -> Box155
FEATURE [Part::Box] Box164  label="Cube144"
  AttacherType = Attacher::AttachEngine3D
  Height = 7
  Length = 5
  Placement = pos=(-5,0,-2) rot=(0,0,1;0rad)
  Width = 40
FEATURE [Part::Box] Box165  label="Cube145"
  AttacherType = Attacher::AttachEngine3D
  Height = 7
  Length = 10
  Placement = pos=(-15,6,-2) rot=(0,0,1;0rad)
  Width = 2
FEATURE [Part::Box] Box166  label="Cube146"
  AttacherType = Attacher::AttachEngine3D
  Height = 7
  Length = 10
  Placement = pos=(-15,10,-2) rot=(0,0,1;0rad)
  Width = 2
FEATURE [Part::Box] Box167  label="Cube147"
  AttacherType = Attacher::AttachEngine3D
  Height = 7
  Length = 10
  Placement = pos=(-15,25.4,-2) rot=(0,0,1;0rad)
  Width = 2
FEATURE [Part::Box] Box168  label="Cube148"
  AttacherType = Attacher::AttachEngine3D
  Height = 7
  Length = 10
  Placement = pos=(-15,34.6,-2) rot=(0,0,1;0rad)
  Width = 2
FEATURE [Part::Sphere] Sphere055
  Angle1 = -90
  Angle2 = 90
  Angle3 = 360
  AttacherType = Attacher::AttachEngine3D
  Placement = pos=(-7.5,6.5,0.5) rot=(0,0,1;0rad)
  Radius = 1.25
FEATURE [Part::Box] Box169  label="Chamfer Cube002"
  AttacherType = Attacher::AttachEngine3D
  Height = 10
  Length = 13
  Placement = pos=(-11.69,0,-1.19) rot=(0,-1,0;0.785398rad)
  Width = 40
FEATURE [Part::Sphere] Sphere056
  Angle1 = -90
  Angle2 = 90
  Angle3 = 360
  AttacherType = Attacher::AttachEngine3D
  Placement = pos=(-7.5,11.5,0.5) rot=(0,0,1;0rad)
  Radius = 1.25
FEATURE [Part::Sphere] Sphere057
  Angle1 = -90
  Angle2 = 90
  Angle3 = 360
  AttacherType = Attacher::AttachEngine3D
  Placement = pos=(-7.5,28,0.5) rot=(0,0,1;0rad)
  Radius = 1.5
FEATURE [Part::Sphere] Sphere058
  Angle1 = -90
  Angle2 = 90
  Angle3 = 360
  AttacherType = Attacher::AttachEngine3D
  Placement = pos=(-7.5,34,0.5) rot=(0,0,1;0rad)
  Radius = 1.5
FEATURE [Part::Box] Box170  label="Cube149"
  AttacherType = Attacher::AttachEngine3D
  Height = 7
  Length = 4
  Placement = pos=(-6,5,-2) rot=(0,0,1;0rad)
  Width = 1
FEATURE [Part::Box] Box171  label="Cube150"
  AttacherType = Attacher::AttachEngine3D
  Height = 7
  Length = 4
  Placement = pos=(-6,8,-2) rot=(0,0,1;0rad)
  Width = 2
FEATURE [Part::Box] Box172  label="Cube151"
  AttacherType = Attacher::AttachEngine3D
  Height = 7
  Length = 4
  Placement = pos=(-6,12,-2) rot=(0,0,1;0rad)
  Width = 1
FEATURE [Part::Box] Box173  label="Cube152"
  AttacherType = Attacher::AttachEngine3D
  Height = 7
  Length = 4
  Placement = pos=(-6,24.4,-2) rot=(0,0,1;0rad)
  Width = 1
FEATURE [Part::Box] Box174  label="Cube153"
  AttacherType = Attacher::AttachEngine3D
  Height = 7
  Length = 4
  Placement = pos=(-6,36.6,-2) rot=(0,0,1;0rad)
  Width = 1
FEATURE [Part::Box] Box175  label="Cube154"
  AttacherType = Attacher::AttachEngine3D
  Height = 7
  Length = 4
  Placement = pos=(-6,27.4,-2) rot=(0,0,1;0rad)
  Width = 7.2
FEATURE [Part::MultiFuse] Fusion061  label="Extra Holes for Clips002"
  Shapes = -> [Box175,Box172,Box174,Box171,Box173,Box170]
FEATURE [Part::Box] Box176  label="Re-level Edge Clip Block004"
  AttacherType = Attacher::AttachEngine3D
  Height = 10
  Length = 20
  Placement = pos=(-19,-2,3) rot=(0,0,1;0rad)
  Width = 44
FEATURE [Part::Box] Box177  label="Re-level Edge Clip Block005"
  AttacherType = Attacher::AttachEngine3D
  Height = 10
  Length = 12
  Placement = pos=(-21.5,-2,-7) rot=(0,0,1;0rad)
  Width = 44
FEATURE [Part::Fuse] Fusion062  label="Bumps002"
  Base = -> Sphere055
  Tool = -> Sphere056
FEATURE [Part::Fuse] Fusion063  label="Holes002"
  Base = -> Sphere057
  Tool = -> Sphere058
FEATURE [Part::MultiFuse] Fusion064
  Shapes = -> [Box164,Box165,Box166,Box167,Box168]
FEATURE [Part::Fuse] Fusion065
  Base = -> Fusion062
  Tool = -> Fusion064
FEATURE [Part::Cut] Cut065
  Base = -> Fusion065
  Tool = -> Fusion063
FEATURE [Part::Cut] Cut066
  Base = -> Cut065
  Tool = -> Fusion061
FEATURE [Part::Cut] Cut067
  Base = -> Cut066
  Tool = -> Box176
FEATURE [Part::Cut] Cut068
  Base = -> Cut067
  Tool = -> Box177
FEATURE [Part::Cut] Cut069  label="Edge Clips001"
  Base = -> Cut068
  Placement = pos=(20,-20,0) rot=(0,0,1;1.5708rad)
  Tool = -> Box169
FEATURE [Part::Box] Box178  label="Cube155"
  AttacherType = Attacher::AttachEngine3D
  Height = 7
  Length = 5
  Placement = pos=(-5,0,-2) rot=(0,0,1;0rad)
  Width = 40
FEATURE [Part::Box] Box179  label="Cube156"
  AttacherType = Attacher::AttachEngine3D
  Height = 7
  Length = 10
  Placement = pos=(-15,10,-2) rot=(0,0,1;0rad)
  Width = 2
FEATURE [Part::Box] Box180  label="Re-level Edge Clip Block006"
  AttacherType = Attacher::AttachEngine3D
  Height = 10
  Length = 20
  Placement = pos=(-19,-2,3) rot=(0,0,1;0rad)
  Width = 44
FEATURE [Part::Box] Box181  label="Cube157"
  AttacherType = Attacher::AttachEngine3D
  Height = 7
  Length = 4
  Placement = pos=(-6,27.4,-2) rot=(0,0,1;0rad)
  Width = 7.2
FEATURE [Part::Box] Box182  label="Cube158"
  AttacherType = Attacher::AttachEngine3D
  Height = 7
  Length = 4
  Placement = pos=(-6,12,-2) rot=(0,0,1;0rad)
  Width = 1
FEATURE [Part::Sphere] Sphere059
  Angle1 = -90
  Angle2 = 90
  Angle3 = 360
  AttacherType = Attacher::AttachEngine3D
  Placement = pos=(-7.5,6.5,0.5) rot=(0,0,1;0rad)
  Radius = 1.25
FEATURE [Part::Box] Box183  label="Cube159"
  AttacherType = Attacher::AttachEngine3D
  Height = 7
  Length = 10
  Placement = pos=(-15,25.4,-2) rot=(0,0,1;0rad)
  Width = 2
FEATURE [Part::Box] Box184  label="Cube160"
  AttacherType = Attacher::AttachEngine3D
  Height = 7
  Length = 4
  Placement = pos=(-6,36.6,-2) rot=(0,0,1;0rad)
  Width = 1
FEATURE [Part::Sphere] Sphere060
  Angle1 = -90
  Angle2 = 90
  Angle3 = 360
  AttacherType = Attacher::AttachEngine3D
  Placement = pos=(-7.5,34,0.5) rot=(0,0,1;0rad)
  Radius = 1.5
FEATURE [Part::Box] Box185  label="Cube161"
  AttacherType = Attacher::AttachEngine3D
  Height = 7
  Length = 4
  Placement = pos=(-6,24.4,-2) rot=(0,0,1;0rad)
  Width = 1
FEATURE [Part::Box] Box186  label="Cube162"
  AttacherType = Attacher::AttachEngine3D
  Height = 7
  Length = 4
  Placement = pos=(-6,8,-2) rot=(0,0,1;0rad)
  Width = 2
FEATURE [Part::Box] Box187  label="Re-level Edge Clip Block007"
  AttacherType = Attacher::AttachEngine3D
  Height = 10
  Length = 12
  Placement = pos=(-21.5,-2,-7) rot=(0,0,1;0rad)
  Width = 44
FEATURE [Part::Sphere] Sphere061
  Angle1 = -90
  Angle2 = 90
  Angle3 = 360
  AttacherType = Attacher::AttachEngine3D
  Placement = pos=(-7.5,11.5,0.5) rot=(0,0,1;0rad)
  Radius = 1.25
FEATURE [Part::Sphere] Sphere062
  Angle1 = -90
  Angle2 = 90
  Angle3 = 360
  AttacherType = Attacher::AttachEngine3D
  Placement = pos=(-7.5,28,0.5) rot=(0,0,1;0rad)
  Radius = 1.5
FEATURE [Part::Fuse] Fusion066  label="Holes003"
  Base = -> Sphere062
  Tool = -> Sphere060
FEATURE [Part::Box] Box188  label="Cube163"
  AttacherType = Attacher::AttachEngine3D
  Height = 7
  Length = 10
  Placement = pos=(-15,34.6,-2) rot=(0,0,1;0rad)
  Width = 2
FEATURE [Part::Box] Box189  label="Cube164"
  AttacherType = Attacher::AttachEngine3D
  Height = 7
  Length = 4
  Placement = pos=(-6,5,-2) rot=(0,0,1;0rad)
  Width = 1
FEATURE [Part::MultiFuse] Fusion067  label="Extra Holes for Clips003"
  Shapes = -> [Box181,Box182,Box184,Box186,Box185,Box189]
FEATURE [Part::Box] Box190  label="Cube165"
  AttacherType = Attacher::AttachEngine3D
  Height = 7
  Length = 10
  Placement = pos=(-15,6,-2) rot=(0,0,1;0rad)
  Width = 2
FEATURE [Part::MultiFuse] Fusion069
  Shapes = -> [Box178,Box190,Box179,Box183,Box188]
FEATURE [Part::Fuse] Fusion070  label="Bumps003"
  Base = -> Sphere059
  Tool = -> Sphere061
FEATURE [Part::Fuse] Fusion068
  Base = -> Fusion070
  Tool = -> Fusion069
FEATURE [Part::Cut] Cut073
  Base = -> Fusion068
  Tool = -> Fusion066
FEATURE [Part::Cut] Cut070
  Base = -> Cut073
  Tool = -> Fusion067
FEATURE [Part::Cut] Cut071
  Base = -> Cut070
  Tool = -> Box180
FEATURE [Part::Cut] Cut072
  Base = -> Cut071
  Tool = -> Box187
FEATURE [Part::Box] Box191  label="Chamfer Cube003"
  AttacherType = Attacher::AttachEngine3D
  Height = 10
  Length = 13
  Placement = pos=(-11.69,0,-1.19) rot=(0,-1,0;0.785398rad)
  Width = 40
FEATURE [Part::Cut] Cut074  label="Edge Clips002"
  Base = -> Cut072
  Placement = pos=(20,20,0) rot=(0,0,1;3.14159rad)
  Tool = -> Box191
FEATURE [Part::Box] Box192  label="Cube166"
  AttacherType = Attacher::AttachEngine3D
  Height = 7
  Length = 10
  Placement = pos=(-15,6,-2) rot=(0,0,1;0rad)
  Width = 2
FEATURE [Part::Box] Box193  label="Chamfer Cube004"
  AttacherType = Attacher::AttachEngine3D
  Height = 10
  Length = 13
  Placement = pos=(-11.69,0,-1.19) rot=(0,-1,0;0.785398rad)
  Width = 40
FEATURE [Part::Box] Box194  label="Re-level Edge Clip Block008"
  AttacherType = Attacher::AttachEngine3D
  Height = 10
  Length = 20
  Placement = pos=(-19,-2,3) rot=(0,0,1;0rad)
  Width = 44
FEATURE [Part::Box] Box195  label="Cube167"
  AttacherType = Attacher::AttachEngine3D
  Height = 7
  Length = 10
  Placement = pos=(-15,10,-2) rot=(0,0,1;0rad)
  Width = 2
FEATURE [Part::Box] Box196  label="Cube168"
  AttacherType = Attacher::AttachEngine3D
  Height = 7
  Length = 5
  Placement = pos=(-5,0,-2) rot=(0,0,1;0rad)
  Width = 40
FEATURE [Part::Box] Box197  label="Cube169"
  AttacherType = Attacher::AttachEngine3D
  Height = 7
  Length = 4
  Placement = pos=(-6,5,-2) rot=(0,0,1;0rad)
  Width = 1
FEATURE [Part::Box] Box198  label="Cube170"
  AttacherType = Attacher::AttachEngine3D
  Height = 7
  Length = 4
  Placement = pos=(-6,12,-2) rot=(0,0,1;0rad)
  Width = 1
FEATURE [Part::Box] Box199  label="Cube171"
  AttacherType = Attacher::AttachEngine3D
  Height = 7
  Length = 4
  Placement = pos=(-6,27.4,-2) rot=(0,0,1;0rad)
  Width = 7.2
FEATURE [Part::Box] Box200  label="Cube172"
  AttacherType = Attacher::AttachEngine3D
  Height = 7
  Length = 4
  Placement = pos=(-6,24.4,-2) rot=(0,0,1;0rad)
  Width = 1
FEATURE [Part::Sphere] Sphere063
  Angle1 = -90
  Angle2 = 90
  Angle3 = 360
  AttacherType = Attacher::AttachEngine3D
  Placement = pos=(-7.5,28,0.5) rot=(0,0,1;0rad)
  Radius = 1.5
FEATURE [Part::Sphere] Sphere064
  Angle1 = -90
  Angle2 = 90
  Angle3 = 360
  AttacherType = Attacher::AttachEngine3D
  Placement = pos=(-7.5,11.5,0.5) rot=(0,0,1;0rad)
  Radius = 1.25
FEATURE [Part::Box] Box201  label="Cube173"
  AttacherType = Attacher::AttachEngine3D
  Height = 7
  Length = 4
  Placement = pos=(-6,8,-2) rot=(0,0,1;0rad)
  Width = 2
FEATURE [Part::Box] Box202  label="Cube174"
  AttacherType = Attacher::AttachEngine3D
  Height = 7
  Length = 10
  Placement = pos=(-15,25.4,-2) rot=(0,0,1;0rad)
  Width = 2
FEATURE [Part::Sphere] Sphere065
  Angle1 = -90
  Angle2 = 90
  Angle3 = 360
  AttacherType = Attacher::AttachEngine3D
  Placement = pos=(-7.5,6.5,0.5) rot=(0,0,1;0rad)
  Radius = 1.25
FEATURE [Part::Fuse] Fusion073  label="Bumps004"
  Base = -> Sphere065
  Tool = -> Sphere064
FEATURE [Part::Sphere] Sphere066
  Angle1 = -90
  Angle2 = 90
  Angle3 = 360
  AttacherType = Attacher::AttachEngine3D
  Placement = pos=(-7.5,34,0.5) rot=(0,0,1;0rad)
  Radius = 1.5
FEATURE [Part::Fuse] Fusion071  label="Holes004"
  Base = -> Sphere063
  Tool = -> Sphere066
FEATURE [Part::Box] Box203  label="Re-level Edge Clip Block009"
  AttacherType = Attacher::AttachEngine3D
  Height = 10
  Length = 12
  Placement = pos=(-21.5,-2,-7) rot=(0,0,1;0rad)
  Width = 44
FEATURE [Part::Box] Box204  label="Cube175"
  AttacherType = Attacher::AttachEngine3D
  Height = 7
  Length = 4
  Placement = pos=(-6,36.6,-2) rot=(0,0,1;0rad)
  Width = 1
FEATURE [Part::MultiFuse] Fusion074  label="Extra Holes for Clips004"
  Shapes = -> [Box199,Box198,Box204,Box201,Box200,Box197]
FEATURE [Part::Box] Box205  label="Cube176"
  AttacherType = Attacher::AttachEngine3D
  Height = 7
  Length = 10
  Placement = pos=(-15,34.6,-2) rot=(0,0,1;0rad)
  Width = 2
FEATURE [Part::MultiFuse] Fusion072
  Shapes = -> [Box196,Box192,Box195,Box202,Box205]
FEATURE [Part::Fuse] Fusion075
  Base = -> Fusion073
  Tool = -> Fusion072
FEATURE [Part::Cut] Cut075
  Base = -> Fusion075
  Tool = -> Fusion071
FEATURE [Part::Cut] Cut076
  Base = -> Cut075
  Tool = -> Fusion074
FEATURE [Part::Cut] Cut078
  Base = -> Cut076
  Tool = -> Box194
FEATURE [Part::Cut] Cut077
  Base = -> Cut078
  Tool = -> Box203
FEATURE [Part::Cut] Cut079  label="Edge Clips003"
  Base = -> Cut077
  Placement = pos=(-20,20,0) rot=(0,0,-1;1.5708rad)
  Tool = -> Box193
FEATURE [Part::MultiFuse] Fusion076  label="Edge Clips Fusion"
  Shapes = -> [Cut059,Cut069,Cut074,Cut079]
FEATURE [Part::Box] Box206  label="Cube177"
  AttacherType = Attacher::AttachEngine3D
  Height = 10
  Length = 10
  Placement = pos=(26,4,1) rot=(0.442189,-0.287968,0.849437;1.66134rad)
  Width = 15
FEATURE [Part::Box] Box207  label="Cube178"
  AttacherType = Attacher::AttachEngine3D
  Height = 10
  Length = 10
  Placement = pos=(-4,26,1) rot=(0.381439,0.080566,0.920876;3.07487rad)
  Width = 15
FEATURE [Part::Box] Box208  label="Cube179"
  AttacherType = Attacher::AttachEngine3D
  Height = 10
  Length = 10
  Placement = pos=(-26,-4,1) rot=(-0.273007,-0.419215,-0.865867;1.78566rad)
  Width = 15
FEATURE [Part::MultiFuse] Fusion078  label="Glue Dents"
  Shapes = -> [Box086,Box208,Box207,Box206]
FEATURE [Part::Box] Box209  label="Cube180"
  AttacherType = Attacher::AttachEngine3D
  Height = 7
  Length = 5
  Placement = pos=(-5,0,-2) rot=(0,0,1;0rad)
  Width = 40
FEATURE [Part::Box] Box210  label="Cube181"
  AttacherType = Attacher::AttachEngine3D
  Height = 7
  Length = 10
  Placement = pos=(-15,6,-2) rot=(0,0,1;0rad)
  Width = 2
FEATURE [Part::Box] Box211  label="Cube182"
  AttacherType = Attacher::AttachEngine3D
  Height = 7
  Length = 10
  Placement = pos=(-15,10,-2) rot=(0,0,1;0rad)
  Width = 2
FEATURE [Part::Box] Box212  label="Cube183"
  AttacherType = Attacher::AttachEngine3D
  Height = 7
  Length = 10
  Placement = pos=(-15,25.4,-2) rot=(0,0,1;0rad)
  Width = 2
FEATURE [Part::Box] Box213  label="Cube184"
  AttacherType = Attacher::AttachEngine3D
  Height = 7
  Length = 10
  Placement = pos=(-15,34.6,-2) rot=(0,0,1;0rad)
  Width = 2
FEATURE [Part::Sphere] Sphere067
  Angle1 = -90
  Angle2 = 90
  Angle3 = 360
  AttacherType = Attacher::AttachEngine3D
  Placement = pos=(-7.5,6.5,0.5) rot=(0,0,1;0rad)
  Radius = 1.25
FEATURE [Part::Box] Box214  label="Chamfer Cube005"
  AttacherType = Attacher::AttachEngine3D
  Height = 10
  Length = 13
  Placement = pos=(-11.69,0,-1.19) rot=(0,-1,0;0.785398rad)
  Width = 40
FEATURE [Part::Sphere] Sphere068
  Angle1 = -90
  Angle2 = 90
  Angle3 = 360
  AttacherType = Attacher::AttachEngine3D
  Placement = pos=(-7.5,11.5,0.5) rot=(0,0,1;0rad)
  Radius = 1.25
FEATURE [Part::Sphere] Sphere069
  Angle1 = -90
  Angle2 = 90
  Angle3 = 360
  AttacherType = Attacher::AttachEngine3D
  Placement = pos=(-7.5,28,0.5) rot=(0,0,1;0rad)
  Radius = 1.5
FEATURE [Part::Sphere] Sphere070
  Angle1 = -90
  Angle2 = 90
  Angle3 = 360
  AttacherType = Attacher::AttachEngine3D
  Placement = pos=(-7.5,34,0.5) rot=(0,0,1;0rad)
  Radius = 1.5
FEATURE [Part::Box] Box215  label="Cube185"
  AttacherType = Attacher::AttachEngine3D
  Height = 7
  Length = 4
  Placement = pos=(-6,5,-2) rot=(0,0,1;0rad)
  Width = 1
FEATURE [Part::Box] Box216  label="Cube186"
  AttacherType = Attacher::AttachEngine3D
  Height = 7
  Length = 4
  Placement = pos=(-6,8,-2) rot=(0,0,1;0rad)
  Width = 2
FEATURE [Part::Box] Box217  label="Cube187"
  AttacherType = Attacher::AttachEngine3D
  Height = 7
  Length = 4
  Placement = pos=(-6,12,-2) rot=(0,0,1;0rad)
  Width = 1
FEATURE [Part::Box] Box218  label="Cube188"
  AttacherType = Attacher::AttachEngine3D
  Height = 7
  Length = 4
  Placement = pos=(-6,24.4,-2) rot=(0,0,1;0rad)
  Width = 1
FEATURE [Part::Box] Box219  label="Cube189"
  AttacherType = Attacher::AttachEngine3D
  Height = 7
  Length = 4
  Placement = pos=(-6,36.6,-2) rot=(0,0,1;0rad)
  Width = 1
FEATURE [Part::Box] Box220  label="Cube190"
  AttacherType = Attacher::AttachEngine3D
  Height = 7
  Length = 4
  Placement = pos=(-6,27.4,-2) rot=(0,0,1;0rad)
  Width = 7.2
FEATURE [Part::MultiFuse] Fusion079  label="Extra Holes for Clips005"
  Shapes = -> [Box220,Box217,Box219,Box216,Box218,Box215]
FEATURE [Part::Box] Box221  label="Re-level Edge Clip Block010"
  AttacherType = Attacher::AttachEngine3D
  Height = 10
  Length = 20
  Placement = pos=(-19,-2,3) rot=(0,0,1;0rad)
  Width = 44
FEATURE [Part::Box] Box222  label="Re-level Edge Clip Block011"
  AttacherType = Attacher::AttachEngine3D
  Height = 10
  Length = 12
  Placement = pos=(-21.5,-2,-7) rot=(0,0,1;0rad)
  Width = 44
FEATURE [Part::Fuse] Fusion080  label="Bumps005"
  Base = -> Sphere067
  Tool = -> Sphere068
FEATURE [Part::Fuse] Fusion081  label="Holes005"
  Base = -> Sphere069
  Tool = -> Sphere070
FEATURE [Part::MultiFuse] Fusion082
  Shapes = -> [Box209,Box210,Box211,Box212,Box213]
FEATURE [Part::Fuse] Fusion083
  Base = -> Fusion080
  Tool = -> Fusion082
FEATURE [Part::Cut] Cut082
  Base = -> Fusion083
  Tool = -> Fusion081
FEATURE [Part::Cut] Cut083
  Base = -> Cut082
  Tool = -> Fusion079
FEATURE [Part::Cut] Cut084
  Base = -> Cut083
  Tool = -> Box221
FEATURE [Part::Cut] Cut085
  Base = -> Cut084
  Tool = -> Box222
FEATURE [Part::Cut] Cut086  label="Edge Clips Master001"
  Base = -> Cut085
  Placement = pos=(-20,-20,0) rot=(0,0,1;0rad)
  Tool = -> Box214
FEATURE [Part::Box] Box223  label="Cube191"
  AttacherType = Attacher::AttachEngine3D
  Height = 7
  Length = 5
  Placement = pos=(-5,0,-2) rot=(0,0,1;0rad)
  Width = 40
FEATURE [Part::Box] Box224  label="Cube192"
  AttacherType = Attacher::AttachEngine3D
  Height = 7
  Length = 4
  Placement = pos=(-6,8,-2) rot=(0,0,1;0rad)
  Width = 2
FEATURE [Part::Box] Box225  label="Chamfer Cube006"
  AttacherType = Attacher::AttachEngine3D
  Height = 10
  Length = 13
  Placement = pos=(-11.69,0,-1.19) rot=(0,-1,0;0.785398rad)
  Width = 40
FEATURE [Part::Box] Box226  label="Cube193"
  AttacherType = Attacher::AttachEngine3D
  Height = 7
  Length = 10
  Placement = pos=(-15,6,-2) rot=(0,0,1;0rad)
  Width = 2
FEATURE [Part::Sphere] Sphere071
  Angle1 = -90
  Angle2 = 90
  Angle3 = 360
  AttacherType = Attacher::AttachEngine3D
  Placement = pos=(-7.5,11.5,0.5) rot=(0,0,1;0rad)
  Radius = 1.25
FEATURE [Part::Box] Box227  label="Cube194"
  AttacherType = Attacher::AttachEngine3D
  Height = 7
  Length = 4
  Placement = pos=(-6,27.4,-2) rot=(0,0,1;0rad)
  Width = 7.2
FEATURE [Part::Box] Box228  label="Cube195"
  AttacherType = Attacher::AttachEngine3D
  Height = 7
  Length = 4
  Placement = pos=(-6,12,-2) rot=(0,0,1;0rad)
  Width = 1
FEATURE [Part::Box] Box229  label="Cube196"
  AttacherType = Attacher::AttachEngine3D
  Height = 7
  Length = 4
  Placement = pos=(-6,24.4,-2) rot=(0,0,1;0rad)
  Width = 1
FEATURE [Part::Sphere] Sphere072
  Angle1 = -90
  Angle2 = 90
  Angle3 = 360
  AttacherType = Attacher::AttachEngine3D
  Placement = pos=(-7.5,6.5,0.5) rot=(0,0,1;0rad)
  Radius = 1.25
FEATURE [Part::Box] Box230  label="Cube197"
  AttacherType = Attacher::AttachEngine3D
  Height = 7
  Length = 4
  Placement = pos=(-6,36.6,-2) rot=(0,0,1;0rad)
  Width = 1
FEATURE [Part::Box] Box231  label="Cube198"
  AttacherType = Attacher::AttachEngine3D
  Height = 7
  Length = 10
  Placement = pos=(-15,10,-2) rot=(0,0,1;0rad)
  Width = 2
FEATURE [Part::Sphere] Sphere073
  Angle1 = -90
  Angle2 = 90
  Angle3 = 360
  AttacherType = Attacher::AttachEngine3D
  Placement = pos=(-7.5,34,0.5) rot=(0,0,1;0rad)
  Radius = 1.5
FEATURE [Part::Box] Box232  label="Cube199"
  AttacherType = Attacher::AttachEngine3D
  Height = 7
  Length = 4
  Placement = pos=(-6,5,-2) rot=(0,0,1;0rad)
  Width = 1
FEATURE [Part::MultiFuse] Fusion085  label="Extra Holes for Clips006"
  Shapes = -> [Box227,Box228,Box230,Box224,Box229,Box232]
FEATURE [Part::Box] Box233  label="Re-level Edge Clip Block012"
  AttacherType = Attacher::AttachEngine3D
  Height = 10
  Length = 20
  Placement = pos=(-19,-2,3) rot=(0,0,1;0rad)
  Width = 44
FEATURE [Part::Box] Box234  label="Cube200"
  AttacherType = Attacher::AttachEngine3D
  Height = 7
  Length = 10
  Placement = pos=(-15,34.6,-2) rot=(0,0,1;0rad)
  Width = 2
FEATURE [Part::Box] Box235  label="Cube201"
  AttacherType = Attacher::AttachEngine3D
  Height = 7
  Length = 10
  Placement = pos=(-15,25.4,-2) rot=(0,0,1;0rad)
  Width = 2
FEATURE [Part::MultiFuse] Fusion086
  Shapes = -> [Box223,Box226,Box231,Box235,Box234]
FEATURE [Part::Fuse] Fusion087  label="Bumps006"
  Base = -> Sphere072
  Tool = -> Sphere071
FEATURE [Part::Fuse] Fusion084
  Base = -> Fusion087
  Tool = -> Fusion086
FEATURE [Part::Sphere] Sphere074
  Angle1 = -90
  Angle2 = 90
  Angle3 = 360
  AttacherType = Attacher::AttachEngine3D
  Placement = pos=(-7.5,28,0.5) rot=(0,0,1;0rad)
  Radius = 1.5
FEATURE [Part::Fuse] Fusion088  label="Holes006"
  Base = -> Sphere074
  Tool = -> Sphere073
FEATURE [Part::Box] Box236  label="Re-level Edge Clip Block013"
  AttacherType = Attacher::AttachEngine3D
  Height = 10
  Length = 12
  Placement = pos=(-21.5,-2,-7) rot=(0,0,1;0rad)
  Width = 44
FEATURE [Part::Cut] Cut087
  Base = -> Fusion084
  Tool = -> Fusion088
FEATURE [Part::Cut] Cut088
  Base = -> Cut087
  Tool = -> Fusion085
FEATURE [Part::Cut] Cut089
  Base = -> Cut088
  Tool = -> Box233
FEATURE [Part::Cut] Cut090
  Base = -> Cut089
  Tool = -> Box236
FEATURE [Part::Cut] Cut091  label="Edge Clips004"
  Base = -> Cut090
  Placement = pos=(20,-20,0) rot=(0,0,1;1.5708rad)
  Tool = -> Box225
FEATURE [Part::Box] Box237  label="Re-level Edge Clip Block014"
  AttacherType = Attacher::AttachEngine3D
  Height = 10
  Length = 12
  Placement = pos=(-21.5,-2,-7) rot=(0,0,1;0rad)
  Width = 44
FEATURE [Part::Box] Box238  label="Cube202"
  AttacherType = Attacher::AttachEngine3D
  Height = 7
  Length = 4
  Placement = pos=(-6,36.6,-2) rot=(0,0,1;0rad)
  Width = 1
FEATURE [Part::Box] Box239  label="Cube203"
  AttacherType = Attacher::AttachEngine3D
  Height = 7
  Length = 10
  Placement = pos=(-15,10,-2) rot=(0,0,1;0rad)
  Width = 2
FEATURE [Part::Box] Box240  label="Cube204"
  AttacherType = Attacher::AttachEngine3D
  Height = 7
  Length = 10
  Placement = pos=(-15,25.4,-2) rot=(0,0,1;0rad)
  Width = 2
FEATURE [Part::Box] Box241  label="Re-level Edge Clip Block015"
  AttacherType = Attacher::AttachEngine3D
  Height = 10
  Length = 20
  Placement = pos=(-19,-2,3) rot=(0,0,1;0rad)
  Width = 44
FEATURE [Part::Box] Box242  label="Cube205"
  AttacherType = Attacher::AttachEngine3D
  Height = 7
  Length = 10
  Placement = pos=(-15,34.6,-2) rot=(0,0,1;0rad)
  Width = 2
FEATURE [Part::Sphere] Sphere075
  Angle1 = -90
  Angle2 = 90
  Angle3 = 360
  AttacherType = Attacher::AttachEngine3D
  Placement = pos=(-7.5,34,0.5) rot=(0,0,1;0rad)
  Radius = 1.5
FEATURE [Part::Sphere] Sphere076
  Angle1 = -90
  Angle2 = 90
  Angle3 = 360
  AttacherType = Attacher::AttachEngine3D
  Placement = pos=(-7.5,28,0.5) rot=(0,0,1;0rad)
  Radius = 1.5
FEATURE [Part::Fuse] Fusion089  label="Holes007"
  Base = -> Sphere076
  Tool = -> Sphere075
FEATURE [Part::Box] Box243  label="Cube206"
  AttacherType = Attacher::AttachEngine3D
  Height = 7
  Length = 4
  Placement = pos=(-6,5,-2) rot=(0,0,1;0rad)
  Width = 1
FEATURE [Part::Box] Box244  label="Cube207"
  AttacherType = Attacher::AttachEngine3D
  Height = 7
  Length = 4
  Placement = pos=(-6,24.4,-2) rot=(0,0,1;0rad)
  Width = 1
FEATURE [Part::Sphere] Sphere077
  Angle1 = -90
  Angle2 = 90
  Angle3 = 360
  AttacherType = Attacher::AttachEngine3D
  Placement = pos=(-7.5,11.5,0.5) rot=(0,0,1;0rad)
  Radius = 1.25
FEATURE [Part::Box] Box245  label="Cube208"
  AttacherType = Attacher::AttachEngine3D
  Height = 7
  Length = 4
  Placement = pos=(-6,12,-2) rot=(0,0,1;0rad)
  Width = 1
FEATURE [Part::Box] Box246  label="Chamfer Cube007"
  AttacherType = Attacher::AttachEngine3D
  Height = 10
  Length = 13
  Placement = pos=(-11.69,0,-1.19) rot=(0,-1,0;0.785398rad)
  Width = 40
FEATURE [Part::Sphere] Sphere078
  Angle1 = -90
  Angle2 = 90
  Angle3 = 360
  AttacherType = Attacher::AttachEngine3D
  Placement = pos=(-7.5,6.5,0.5) rot=(0,0,1;0rad)
  Radius = 1.25
FEATURE [Part::Fuse] Fusion090  label="Bumps007"
  Base = -> Sphere078
  Tool = -> Sphere077
FEATURE [Part::Box] Box247  label="Cube209"
  AttacherType = Attacher::AttachEngine3D
  Height = 7
  Length = 5
  Placement = pos=(-5,0,-2) rot=(0,0,1;0rad)
  Width = 40
FEATURE [Part::Box] Box248  label="Cube210"
  AttacherType = Attacher::AttachEngine3D
  Height = 7
  Length = 4
  Placement = pos=(-6,27.4,-2) rot=(0,0,1;0rad)
  Width = 7.2
FEATURE [Part::Box] Box249  label="Cube211"
  AttacherType = Attacher::AttachEngine3D
  Height = 7
  Length = 4
  Placement = pos=(-6,8,-2) rot=(0,0,1;0rad)
  Width = 2
FEATURE [Part::MultiFuse] Fusion091  label="Extra Holes for Clips007"
  Shapes = -> [Box248,Box245,Box238,Box249,Box244,Box243]
FEATURE [Part::Box] Box250  label="Cube212"
  AttacherType = Attacher::AttachEngine3D
  Height = 7
  Length = 10
  Placement = pos=(-15,6,-2) rot=(0,0,1;0rad)
  Width = 2
FEATURE [Part::MultiFuse] Fusion092
  Shapes = -> [Box247,Box250,Box239,Box240,Box242]
FEATURE [Part::Fuse] Fusion093
  Base = -> Fusion090
  Tool = -> Fusion092
FEATURE [Part::Cut] Cut093
  Base = -> Fusion093
  Tool = -> Fusion089
FEATURE [Part::Cut] Cut094
  Base = -> Cut093
  Tool = -> Fusion091
FEATURE [Part::Cut] Cut095
  Base = -> Cut094
  Tool = -> Box241
FEATURE [Part::Cut] Cut096
  Base = -> Cut095
  Tool = -> Box237
FEATURE [Part::Cut] Cut092  label="Edge Clips005"
  Base = -> Cut096
  Placement = pos=(20,20,0) rot=(0,0,1;3.14159rad)
  Tool = -> Box246
FEATURE [Part::Box] Box251  label="Re-level Edge Clip Block016"
  AttacherType = Attacher::AttachEngine3D
  Height = 10
  Length = 12
  Placement = pos=(-21.5,-2,-7) rot=(0,0,1;0rad)
  Width = 44
FEATURE [Part::Box] Box252  label="Cube213"
  AttacherType = Attacher::AttachEngine3D
  Height = 7
  Length = 10
  Placement = pos=(-15,10,-2) rot=(0,0,1;0rad)
  Width = 2
FEATURE [Part::Box] Box253  label="Cube214"
  AttacherType = Attacher::AttachEngine3D
  Height = 7
  Length = 4
  Placement = pos=(-6,12,-2) rot=(0,0,1;0rad)
  Width = 1
FEATURE [Part::Box] Box254  label="Chamfer Cube008"
  AttacherType = Attacher::AttachEngine3D
  Height = 10
  Length = 13
  Placement = pos=(-11.69,0,-1.19) rot=(0,-1,0;0.785398rad)
  Width = 40
FEATURE [Part::Sphere] Sphere079
  Angle1 = -90
  Angle2 = 90
  Angle3 = 360
  AttacherType = Attacher::AttachEngine3D
  Placement = pos=(-7.5,6.5,0.5) rot=(0,0,1;0rad)
  Radius = 1.25
FEATURE [Part::Box] Box255  label="Cube215"
  AttacherType = Attacher::AttachEngine3D
  Height = 7
  Length = 5
  Placement = pos=(-5,0,-2) rot=(0,0,1;0rad)
  Width = 40
FEATURE [Part::Box] Box256  label="Cube216"
  AttacherType = Attacher::AttachEngine3D
  Height = 7
  Length = 4
  Placement = pos=(-6,27.4,-2) rot=(0,0,1;0rad)
  Width = 7.2
FEATURE [Part::Box] Box257  label="Cube217"
  AttacherType = Attacher::AttachEngine3D
  Height = 7
  Length = 4
  Placement = pos=(-6,8,-2) rot=(0,0,1;0rad)
  Width = 2
FEATURE [Part::Box] Box258  label="Cube218"
  AttacherType = Attacher::AttachEngine3D
  Height = 7
  Length = 10
  Placement = pos=(-15,6,-2) rot=(0,0,1;0rad)
  Width = 2
FEATURE [Part::Sphere] Sphere080
  Angle1 = -90
  Angle2 = 90
  Angle3 = 360
  AttacherType = Attacher::AttachEngine3D
  Placement = pos=(-7.5,28,0.5) rot=(0,0,1;0rad)
  Radius = 1.5
FEATURE [Part::Box] Box259  label="Cube219"
  AttacherType = Attacher::AttachEngine3D
  Height = 7
  Length = 4
  Placement = pos=(-6,5,-2) rot=(0,0,1;0rad)
  Width = 1
FEATURE [Part::Box] Box260  label="Cube220"
  AttacherType = Attacher::AttachEngine3D
  Height = 7
  Length = 4
  Placement = pos=(-6,24.4,-2) rot=(0,0,1;0rad)
  Width = 1
FEATURE [Part::Sphere] Sphere081
  Angle1 = -90
  Angle2 = 90
  Angle3 = 360
  AttacherType = Attacher::AttachEngine3D
  Placement = pos=(-7.5,11.5,0.5) rot=(0,0,1;0rad)
  Radius = 1.25
FEATURE [Part::Box] Box261  label="Re-level Edge Clip Block017"
  AttacherType = Attacher::AttachEngine3D
  Height = 10
  Length = 20
  Placement = pos=(-19,-2,3) rot=(0,0,1;0rad)
  Width = 44
FEATURE [Part::Box] Box262  label="Cube221"
  AttacherType = Attacher::AttachEngine3D
  Height = 7
  Length = 10
  Placement = pos=(-15,34.6,-2) rot=(0,0,1;0rad)
  Width = 2
FEATURE [Part::Box] Box263  label="Cube222"
  AttacherType = Attacher::AttachEngine3D
  Height = 7
  Length = 10
  Placement = pos=(-15,25.4,-2) rot=(0,0,1;0rad)
  Width = 2
FEATURE [Part::MultiFuse] Fusion096
  Shapes = -> [Box255,Box258,Box252,Box263,Box262]
FEATURE [Part::Box] Box264  label="Cube223"
  AttacherType = Attacher::AttachEngine3D
  Height = 7
  Length = 4
  Placement = pos=(-6,36.6,-2) rot=(0,0,1;0rad)
  Width = 1
FEATURE [Part::MultiFuse] Fusion095  label="Extra Holes for Clips008"
  Shapes = -> [Box256,Box253,Box264,Box257,Box260,Box259]
FEATURE [Part::Fuse] Fusion098  label="Bumps008"
  Base = -> Sphere079
  Tool = -> Sphere081
FEATURE [Part::Fuse] Fusion094
  Base = -> Fusion098
  Tool = -> Fusion096
FEATURE [Part::Sphere] Sphere082
  Angle1 = -90
  Angle2 = 90
  Angle3 = 360
  AttacherType = Attacher::AttachEngine3D
  Placement = pos=(-7.5,34,0.5) rot=(0,0,1;0rad)
  Radius = 1.5
FEATURE [Part::Fuse] Fusion097  label="Holes008"
  Base = -> Sphere080
  Tool = -> Sphere082
FEATURE [Part::Cut] Cut101
  Base = -> Fusion094
  Tool = -> Fusion097
FEATURE [Part::Cut] Cut097
  Base = -> Cut101
  Tool = -> Fusion095
FEATURE [Part::Cut] Cut098
  Base = -> Cut097
  Tool = -> Box261
FEATURE [Part::Cut] Cut099
  Base = -> Cut098
  Tool = -> Box251
FEATURE [Part::Cut] Cut100  label="Edge Clips006"
  Base = -> Cut099
  Placement = pos=(-20,20,0) rot=(0,0,-1;1.5708rad)
  Tool = -> Box254
FEATURE [Part::Box] Box265  label="Cube224"
  AttacherType = Attacher::AttachEngine3D
  Height = 10
  Length = 10
  Placement = pos=(4,-26,1) rot=(0.205904,-0.974848,-0.085288;0.803573rad)
  Width = 15
FEATURE [Part::Box] Box266  label="Cube225"
  AttacherType = Attacher::AttachEngine3D
  Height = 10
  Length = 10
  Placement = pos=(-26,-4,1) rot=(-0.273007,-0.419215,-0.865867;1.78566rad)
  Width = 15
FEATURE [Part::Box] Box267  label="Cube226"
  AttacherType = Attacher::AttachEngine3D
  Height = 10
  Length = 10
  Placement = pos=(-4,26,1) rot=(0.381439,0.080566,0.920876;3.07487rad)
  Width = 15
FEATURE [Part::Box] Box268  label="Cube227"
  AttacherType = Attacher::AttachEngine3D
  Height = 10
  Length = 10
  Placement = pos=(26,4,1) rot=(0.442189,-0.287968,0.849437;1.66134rad)
  Width = 15
FEATURE [Part::MultiFuse] Fusion099  label="Glue Dents001"
  Shapes = -> [Box265,Box266,Box267,Box268]
FEATURE [Part::MultiFuse] Fusion100  label="Edge Clips Fusion001"
  Shapes = -> [Cut100,Cut086,Cut091,Cut092]
FEATURE [Drawing::FeatureViewAnnotation] Annotation001
  Font = Sans
  Rotation = 0
  Scale = 7
  Text = 0.5 rejigged whole thing, stopped clips overhang and moved bump and holes back 0.5
  ViewResult = <g transform="translate(14,30) rotate(0)">\n<text id="Annotation001"\n font-family="Sans"\n font-size="7"\n fill="#000000">\n<tspan x="0" dy="1em">0.5 rejigged whole thing, stopped clips overhang and moved bump and holes back 0.5</tspan>\n</text>\n</g>
  Visible = false
  X = 14
  Y = 30
FEATURE [Part::Cylinder] Cylinder027  label="z-axis"
  Angle = 360
  AttacherType = Attacher::AttachEngine3D
  Height = 73
  Placement = pos=(0,0,-18) rot=(0,0,1;0rad)
  Radius = 0.5
FEATURE [Part::MultiFuse] Fusion101
  Placement = pos=(-15,-15,0) rot=(0,0,1;0rad)
  Shapes = -> [Box069,Cylinder018,Sphere030]
FEATURE [App::DocumentObjectGroup] Group002  label="Old 0.1"
  Group = -> [Sphere027,Sphere028,Sphere029,Sphere031,Sphere032,Sphere033,Sphere034,Cylinder012,Cylinder016,Cylinder015,Cylinder014,Cylinder013,Cylinder017,Cylinder019,Box067,Box073,Box071,Box068,Box070,Box072,Box074]
FEATURE [Part::Box] Box269  label="Square Nut Hole 024"
  AttacherType = Attacher::AttachEngine3D
  Height = 2
  Length = 5.8
  Placement = pos=(-2.9,2.9,2.1) rot=(1,0,0;3.14159rad)
  Width = 5.8
FEATURE [Part::Cylinder] Cylinder028
  Angle = 360
  AttacherType = Attacher::AttachEngine3D
  Height = 10
  Placement = pos=(0,0,6.7) rot=(1,0,0;3.14159rad)
  Radius = 1.7
FEATURE [Part::Sphere] Sphere083
  Angle1 = -90
  Angle2 = 90
  Angle3 = 360
  AttacherType = Attacher::AttachEngine3D
  Placement = pos=(0,0,4.3) rot=(1,0,0;3.14159rad)
  Radius = 3.35
FEATURE [Part::MultiFuse] Fusion102
  Placement = pos=(-15,0,0) rot=(0,0,1;0rad)
  Shapes = -> [Box269,Cylinder028,Sphere083]
FEATURE [Part::Fuse] Fusion103
  Base = -> Fusion101
  Tool = -> Fusion102
FEATURE [Part::Feature] Fusion103001
  Placement = pos=(0,0,0) rot=(0,0,1;1.5708rad)
  shape: bbox 21.7 x 6.7 x 10.95 mm, 18 faces, 2 solids (baked)
FEATURE [Part::Feature] Fusion103002
  Placement = pos=(0,0,0) rot=(0,0,1;3.14159rad)
  shape: bbox 6.7 x 21.7 x 10.95 mm, 18 faces, 2 solids (baked)
FEATURE [Part::Feature] Fusion103003
  Placement = pos=(0,0,0) rot=(0,0,-1;1.5708rad)
  shape: bbox 21.7 x 6.7 x 10.95 mm, 18 faces, 2 solids (baked)
FEATURE [Part::MultiFuse] Fusion103004  label="Nut Holes"
  Shapes = -> [Fusion103,Fusion103001,Fusion103002,Fusion103003]
FEATURE [Part::Fuse] Fusion103005  label="Cube with Edge Clips"
  Base = -> Box075
  Tool = -> Fusion100
FEATURE [Part::Cut] Cut102
  Base = -> Fusion103005
  Tool = -> Fusion099
FEATURE [Part::Cut] Cut103
  Base = -> Cut102
  Tool = -> Fusion103004
FEATURE [Part::Cut] Cut104
  Base = -> Cut103
  Tool = -> Chamfer014
FEATURE [Part::Cut] Cut105
  Base = -> Cut104
  Tool = -> Chamfer013
FEATURE [Part::Cut] Cut106  label="Nut Plate 1.1"
  Base = -> Cut105
  Tool = -> Box145
FEATURE [Part::Fuse] Fusion103006
  Base = -> Cut047
  Tool = -> Fusion076
FEATURE [Part::Cut] Cut107
  Base = -> Fusion103006
  Tool = -> Fusion052
FEATURE [Part::Cut] Cut108
  Base = -> Cut107
  Tool = -> Chamfer008
FEATURE [Part::Cut] Cut109
  Base = -> Cut108
  Tool = -> Box085
FEATURE [Part::Cut] Cut110  label="Ball Plate 1.1"
  Base = -> Cut109
  Tool = -> Fusion078
FEATURE [Drawing::FeatureViewAnnotation] Annotation002
  Font = Sans
  Rotation = 0
  Scale = 7
  ViewResult = <g transform="translate(10,10) rotate(0)">\n<text id="Annotation002"\n font-family="Sans"\n font-size="7"\n fill="#000000">\n<tspan x="0" dy="1em"></tspan>\n</text>\n</g>
  Visible = true
  X = 10
  Y = 10
FEATURE [Drawing::FeatureViewAnnotation] Annotation003
  Font = Sans
  Rotation = 0
  Scale = 7
  Text = 0.5 - > 1.0
  ViewResult = <g transform="translate(14,18) rotate(0)">\n<text id="Annotation003"\n font-family="Sans"\n font-size="7"\n fill="#000000">\n<tspan x="0" dy="1em">0.5 - > 1.0</tspan>\n</text>\n</g>
  Visible = true
  X = 14
  Y = 18
FEATURE [Drawing::FeatureViewAnnotation] Annotation004
  Font = Sans
  Rotation = 0
  Scale = 7
  ViewResult = <g transform="translate(10,10) rotate(0)">\n<text id="Annotation004"\n font-family="Sans"\n font-size="7"\n fill="#000000">\n<tspan x="0" dy="1em"></tspan>\n</text>\n</g>
  Visible = true
  X = 10
  Y = 10
FEATURE [Drawing::FeatureViewAnnotation] Annotation005
  Font = Sans
  Rotation = 0
  Scale = 5
  Text = 0.5 is a working version. 1.0 has everything moved to centre point and then the ball and nut holes moved so that blocks can be mounted in half position
  ViewResult = <g transform="translate(10,30) rotate(0)">\n<text id="Annotation005"\n font-family="Sans"\n font-size="5"\n fill="#000000">\n<tspan x="0" dy="1em">0.5 is a working version. 1.0 has everything moved to centre point and then the ball and nut holes moved so that blocks can be mounted in half position</tspan>\n</text>\n</g>
  Visible = true
  X = 10
  Y = 30
FEATURE [Drawing::FeatureViewAnnotation] Annotation006
  Font = Sans
  Rotation = 0
  Scale = 5
  Text = 1.1 Moved the cube creating the hole with the octagon by 1mm to so distance between pcbs is bigger | Also added holes
  ViewResult = <g transform="translate(10,40) rotate(0)">\n<text id="Annotation006"\n font-family="Sans"\n font-size="5"\n fill="#000000">\n<tspan x="0" dy="1em">1.1 Moved the cube creating the hole with the octagon by 1mm to so distance between pcbs is bigger</tspan>\n<tspan x="0" dy="1em">Also added holes</tspan>\n<tspan x="0" dy="1em"></tspan>\n</text>\n</g>
  Visible = true
  X = 10
  Y = 40
FEATURE [Part::Cylinder] Cylinder029
  Angle = 360
  AttacherType = Attacher::AttachEngine3D
  Height = 10
  Placement = pos=(15,-15,-5) rot=(0,0,1;1.5708rad)
  Radius = 1.7
FEATURE [Part::Sphere] Sphere084  label="Mag Hole001"
  Angle1 = -90
  Angle2 = 90
  Angle3 = 360
  AttacherType = Attacher::AttachEngine3D
  Placement = pos=(15,-15,1.7) rot=(0,0,1;1.5708rad)
  Radius = 2.83
FEATURE [Part::Sphere] Sphere085  label="Mag Hole002"
  Angle1 = -90
  Angle2 = 90
  Angle3 = 360
  AttacherType = Attacher::AttachEngine3D
  Placement = pos=(15,15,1.7) rot=(0,0,1;3.14159rad)
  Radius = 2.83
FEATURE [Part::Sphere] Sphere086  label="Mag Hole 004"
  Angle1 = -90
  Angle2 = 90
  Angle3 = 360
  AttacherType = Attacher::AttachEngine3D
  Placement = pos=(3e-15,15,1.7) rot=(0,0,1;1.5708rad)
  Radius = 2.825
FEATURE [Part::Sphere] Sphere087  label="Mag Hole 005"
  Angle1 = -90
  Angle2 = 90
  Angle3 = 360
  AttacherType = Attacher::AttachEngine3D
  Placement = pos=(-15,2e-15,1.7) rot=(0,0,1;3.14159rad)
  Radius = 2.825
FEATURE [Part::Sphere] Sphere088  label="Mag Hole 006"
  Angle1 = -90
  Angle2 = 90
  Angle3 = 360
  AttacherType = Attacher::AttachEngine3D
  Placement = pos=(-3e-15,-15,1.7) rot=(0,0,-1;1.5708rad)
  Radius = 2.825
FEATURE [Part::Cylinder] Cylinder030
  Angle = 360
  AttacherType = Attacher::AttachEngine3D
  Height = 10
  Placement = pos=(15,15,-5) rot=(0,0,1;3.14159rad)
  Radius = 1.7
FEATURE [Part::Cylinder] Cylinder031
  Angle = 360
  AttacherType = Attacher::AttachEngine3D
  Height = 10
  Placement = pos=(3e-15,15,-5) rot=(0,0,1;1.5708rad)
  Radius = 1.7
FEATURE [Part::Cylinder] Cylinder032
  Angle = 360
  AttacherType = Attacher::AttachEngine3D
  Height = 10
  Placement = pos=(-15,6e-15,-5) rot=(0,0,1;3.14159rad)
  Radius = 1.7
FEATURE [Part::Cylinder] Cylinder033
  Angle = 360
  AttacherType = Attacher::AttachEngine3D
  Height = 10
  Placement = pos=(-9e-15,-15,-5) rot=(0,0,-1;1.5708rad)
  Radius = 1.7
FEATURE [Part::MultiFuse] Fusion103007
  Shapes = -> [Cylinder029,Sphere087,Sphere084,Sphere086,Sphere088,Cylinder032,Cylinder033,Sphere085,Cylinder031,Cylinder030]
FEATURE [Part::Cut] Cut111  label="Ball Plate with Extra Holes"
  Base = -> Cut110
  Tool = -> Fusion103007
FEATURE [Part::Cylinder] Cylinder034
  Angle = 360
  AttacherType = Attacher::AttachEngine3D
  Height = 4
  Placement = pos=(-9.75,-9.75,-3) rot=(0,0,1;0rad)
  Radius = 1.5
FEATURE [Part::Cylinder] Cylinder035
  Angle = 360
  AttacherType = Attacher::AttachEngine3D
  Height = 4
  Placement = pos=(9.75,9.75,-3) rot=(0,0,1;0rad)
  Radius = 1.5
FEATURE [Part::Cylinder] Cylinder036
  Angle = 360
  AttacherType = Attacher::AttachEngine3D
  Height = 4
  Placement = pos=(-9.75,9.75,-3) rot=(0,0,1;0rad)
  Radius = 1.5
FEATURE [Part::Cylinder] Cylinder037
  Angle = 360
  AttacherType = Attacher::AttachEngine3D
  Height = 4
  Placement = pos=(9.75,-9.75,-3) rot=(0,0,1;0rad)
  Radius = 1.5
FEATURE [Part::MultiFuse] Fusion103008
  Shapes = -> [Cylinder034,Cylinder037,Cylinder036,Cylinder035]
FEATURE [Part::Cut] Cut112  label="Ball Plate 1.2"
  Base = -> Cut111
  Tool = -> Fusion103008
FEATURE [Part::Cylinder] Cylinder038
  Angle = 360
  AttacherType = Attacher::AttachEngine3D
  Height = 4
  Placement = pos=(-9.75,-9.75,-3) rot=(0,0,1;0rad)
  Radius = 1.5
FEATURE [Part::Cylinder] Cylinder039
  Angle = 360
  AttacherType = Attacher::AttachEngine3D
  Height = 4
  Placement = pos=(9.75,-9.75,-3) rot=(0,0,1;0rad)
  Radius = 1.5
FEATURE [Part::Cylinder] Cylinder040
  Angle = 360
  AttacherType = Attacher::AttachEngine3D
  Height = 4
  Placement = pos=(-9.75,9.75,-3) rot=(0,0,1;0rad)
  Radius = 1.5
FEATURE [Part::Cylinder] Cylinder041
  Angle = 360
  AttacherType = Attacher::AttachEngine3D
  Height = 4
  Placement = pos=(9.75,9.75,-3) rot=(0,0,1;0rad)
  Radius = 1.5
FEATURE [Part::MultiFuse] Fusion103009
  Shapes = -> [Cylinder038,Cylinder041,Cylinder039,Cylinder040]
FEATURE [Part::Cut] Cut113  label="Nut Plate 1.2"
  Base = -> Cut106
  Tool = -> Fusion103009
FEATURE [Drawing::FeatureViewAnnotation] Annotation007
  Font = Sans
  Rotation = 0
  Scale = 7
  ViewResult = <g transform="translate(10,10) rotate(0)">\n<text id="Annotation007"\n font-family="Sans"\n font-size="7"\n fill="#000000">\n<tspan x="0" dy="1em"></tspan>\n</text>\n</g>
  Visible = true
  X = 10
  Y = 10
FEATURE [Drawing::FeatureViewAnnotation] Annotation008
  Font = Sans
  Rotation = 0
  Scale = 7
  ViewResult = <g transform="translate(10,10) rotate(0)">\n<text id="Annotation008"\n font-family="Sans"\n font-size="7"\n fill="#000000">\n<tspan x="0" dy="1em"></tspan>\n</text>\n</g>
  Visible = true
  X = 10
  Y = 10
FEATURE [Drawing::FeaturePage] Page
  EditableTexts = AUTHOR NAME | CREATION DATE | SUPERVISOR NAME | CHECK DATE | SCALE | WEIGHT | NUMBER | SHEET | TITLE | SUBTITLE
  Group = -> [Annotation,Annotation001,Annotation002,Annotation004,Annotation007,Annotation008]
  Template = <path>
FEATURE [Drawing::FeatureViewAnnotation] Annotation009
  Font = Sans
  Rotation = 0
  Scale = 5
  Text = 1.2 Added holes on the corners of the PCB holes to make it easier to fit
  ViewResult = <g transform="translate(10,50) rotate(0)">\n<text id="Annotation009"\n font-family="Sans"\n font-size="5"\n fill="#000000">\n<tspan x="0" dy="1em">1.1 Moved the cube creating the hole with the octagon by 1mm to so distance between pcbs is bigger</tspan>\n<tspan x="0" dy="1em">Also added holes</tspan>\n<tspan x="0" dy="1em"></tspan>\n</text>\n</g>
  Visible = true
  X = 10
  Y = 50
FEATURE [Drawing::FeaturePage] Page001
  EditableTexts = AUTHOR NAME | CREATION DATE | SUPERVISOR NAME | CHECK DATE | SCALE | WEIGHT | NUMBER | SHEET | TITLE | SUBTITLE
  Group = -> [Annotation003,Annotation005,Annotation006,Annotation009]
  Template = <path>
FEATURE [Part::Feature] Fusion103010
  Placement = pos=(0,0,0) rot=(0,0,-1;1.5708rad)
  shape: bbox 21.7 x 6.7 x 10.95 mm, 18 faces, 2 solids (baked)
FEATURE [Part::Feature] Fusion103011
  Placement = pos=(0,0,0) rot=(0,0,1;3.14159rad)
  shape: bbox 6.7 x 21.7 x 10.95 mm, 18 faces, 2 solids (baked)
FEATURE [Part::Feature] Fusion103012
  Placement = pos=(0,0,0) rot=(0,0,1;1.5708rad)
  shape: bbox 21.7 x 6.7 x 10.95 mm, 18 faces, 2 solids (baked)
FEATURE [Part::Box] Box270  label="Square Nut Hole 025"
  AttacherType = Attacher::AttachEngine3D
  Height = 2
  Length = 5.8
  Placement = pos=(-2.9,2.9,2.1) rot=(1,0,0;3.14159rad)
  Width = 5.8
FEATURE [Part::Cylinder] Cylinder042
  Angle = 360
  AttacherType = Attacher::AttachEngine3D
  Height = 10
  Placement = pos=(0,0,6.7) rot=(1,0,0;3.14159rad)
  Radius = 1.7
FEATURE [Part::Box] Box271  label="Cube228"
  AttacherType = Attacher::AttachEngine3D
  Height = 5
  Length = 40
  Placement = pos=(-20,-20,-2) rot=(0,0,1;0rad)
  Width = 40
FEATURE [Part::Sphere] Sphere089
  Angle1 = -90
  Angle2 = 90
  Angle3 = 360
  AttacherType = Attacher::AttachEngine3D
  Placement = pos=(0,0,4.3) rot=(1,0,0;3.14159rad)
  Radius = 3.35
FEATURE [Part::Box] Box272  label="Cube229"
  AttacherType = Attacher::AttachEngine3D
  Height = 15
  Length = 19.5
  Placement = pos=(-9.75,-9.75,-14) rot=(0,0,1;0rad)
  Width = 19.5
FEATURE [Part::Box] Box273  label="Cube230"
  AttacherType = Attacher::AttachEngine3D
  Height = 15
  Length = 19.5
  Placement = pos=(-9.75,-9.75,-3) rot=(0,0,1;0rad)
  Width = 19.5
FEATURE [Part::Chamfer] Chamfer015  label="Octagon001"
  Base = -> Box273
  Edges = 4 edges r=4: [Edge1,Edge3,Edge5,Edge7]
FEATURE [Part::Box] Box274  label="Cube231"
  AttacherType = Attacher::AttachEngine3D
  Height = 10
  Length = 24
  Placement = pos=(-12,-12,2.1) rot=(0,0,1;0rad)
  Width = 24
FEATURE [Part::Box] Box275  label="Cube232"
  AttacherType = Attacher::AttachEngine3D
  Height = 14
  Length = 20
  Placement = pos=(-10,-10,0) rot=(0,0,1;0rad)
  Width = 20
FEATURE [Part::Cut] Cut116
  Base = -> Box274
  Tool = -> Box275
FEATURE [Part::Chamfer] Chamfer016  label="Glue Channel001"
  Base = -> Cut116
  Edges = 8 edges r=0.95: [Edge4,Edge5,Edge14,Edge16,Edge17,Edge18,Edge19,Edge20]
FEATURE [Part::Box] Box276  label="Cube233"
  AttacherType = Attacher::AttachEngine3D
  Height = 7
  Length = 5
  Placement = pos=(-5,0,-2) rot=(0,0,1;0rad)
  Width = 40
FEATURE [Part::Box] Box277  label="Cube234"
  AttacherType = Attacher::AttachEngine3D
  Height = 7
  Length = 10
  Placement = pos=(-15,6,-2) rot=(0,0,1;0rad)
  Width = 2
FEATURE [Part::Box] Box278  label="Cube235"
  AttacherType = Attacher::AttachEngine3D
  Height = 7
  Length = 10
  Placement = pos=(-15,10,-2) rot=(0,0,1;0rad)
  Width = 2
FEATURE [Part::Box] Box279  label="Cube236"
  AttacherType = Attacher::AttachEngine3D
  Height = 7
  Length = 10
  Placement = pos=(-15,25.4,-2) rot=(0,0,1;0rad)
  Width = 2
FEATURE [Part::Box] Box280  label="Cube237"
  AttacherType = Attacher::AttachEngine3D
  Height = 7
  Length = 10
  Placement = pos=(-15,34.6,-2) rot=(0,0,1;0rad)
  Width = 2
FEATURE [Part::Sphere] Sphere090
  Angle1 = -90
  Angle2 = 90
  Angle3 = 360
  AttacherType = Attacher::AttachEngine3D
  Placement = pos=(-7.5,6.5,0.5) rot=(0,0,1;0rad)
  Radius = 1.25
FEATURE [Part::Box] Box281  label="Chamfer Cube009"
  AttacherType = Attacher::AttachEngine3D
  Height = 10
  Length = 13
  Placement = pos=(-11.69,0,-1.19) rot=(0,-1,0;0.785398rad)
  Width = 40
FEATURE [Part::Sphere] Sphere091
  Angle1 = -90
  Angle2 = 90
  Angle3 = 360
  AttacherType = Attacher::AttachEngine3D
  Placement = pos=(-7.5,11.5,0.5) rot=(0,0,1;0rad)
  Radius = 1.25
FEATURE [Part::Sphere] Sphere092
  Angle1 = -90
  Angle2 = 90
  Angle3 = 360
  AttacherType = Attacher::AttachEngine3D
  Placement = pos=(-7.5,28,0.5) rot=(0,0,1;0rad)
  Radius = 1.5
FEATURE [Part::Sphere] Sphere093
  Angle1 = -90
  Angle2 = 90
  Angle3 = 360
  AttacherType = Attacher::AttachEngine3D
  Placement = pos=(-7.5,34,0.5) rot=(0,0,1;0rad)
  Radius = 1.5
FEATURE [Part::Box] Box282  label="Cube238"
  AttacherType = Attacher::AttachEngine3D
  Height = 7
  Length = 4
  Placement = pos=(-6,5,-2) rot=(0,0,1;0rad)
  Width = 1
FEATURE [Part::Box] Box283  label="Cube239"
  AttacherType = Attacher::AttachEngine3D
  Height = 7
  Length = 4
  Placement = pos=(-6,8,-2) rot=(0,0,1;0rad)
  Width = 2
FEATURE [Part::Box] Box284  label="Cube240"
  AttacherType = Attacher::AttachEngine3D
  Height = 7
  Length = 4
  Placement = pos=(-6,12,-2) rot=(0,0,1;0rad)
  Width = 1
FEATURE [Part::Box] Box285  label="Cube241"
  AttacherType = Attacher::AttachEngine3D
  Height = 7
  Length = 4
  Placement = pos=(-6,24.4,-2) rot=(0,0,1;0rad)
  Width = 1
FEATURE [Part::Box] Box286  label="Cube242"
  AttacherType = Attacher::AttachEngine3D
  Height = 7
  Length = 4
  Placement = pos=(-6,36.6,-2) rot=(0,0,1;0rad)
  Width = 1
FEATURE [Part::Box] Box287  label="Cube243"
  AttacherType = Attacher::AttachEngine3D
  Height = 7
  Length = 4
  Placement = pos=(-6,27.4,-2) rot=(0,0,1;0rad)
  Width = 7.2
FEATURE [Part::MultiFuse] Fusion103013  label="Extra Holes for Clips009"
  Shapes = -> [Box287,Box284,Box286,Box283,Box285,Box282]
FEATURE [Part::Box] Box288  label="Re-level Edge Clip Block018"
  AttacherType = Attacher::AttachEngine3D
  Height = 10
  Length = 20
  Placement = pos=(-19,-2,3) rot=(0,0,1;0rad)
  Width = 44
FEATURE [Part::Box] Box289  label="Re-level Edge Clip Block019"
  AttacherType = Attacher::AttachEngine3D
  Height = 10
  Length = 12
  Placement = pos=(-21.5,-2,-7) rot=(0,0,1;0rad)
  Width = 44
FEATURE [Part::Fuse] Fusion103014  label="Bumps009"
  Base = -> Sphere090
  Tool = -> Sphere091
FEATURE [Part::Fuse] Fusion103015  label="Holes009"
  Base = -> Sphere092
  Tool = -> Sphere093
FEATURE [Part::MultiFuse] Fusion103016
  Shapes = -> [Box276,Box277,Box278,Box279,Box280]
FEATURE [Part::Fuse] Fusion103017
  Base = -> Fusion103014
  Tool = -> Fusion103016
FEATURE [Part::Cut] Cut117
  Base = -> Fusion103017
  Tool = -> Fusion103015
FEATURE [Part::Cut] Cut118
  Base = -> Cut117
  Tool = -> Fusion103013
FEATURE [Part::Cut] Cut119
  Base = -> Cut118
  Tool = -> Box288
FEATURE [Part::Cut] Cut120
  Base = -> Cut119
  Tool = -> Box289
FEATURE [Part::Cut] Cut121  label="Edge Clips Master002"
  Base = -> Cut120
  Placement = pos=(-20,-20,0) rot=(0,0,1;0rad)
  Tool = -> Box281
FEATURE [Part::Box] Box290  label="Cube244"
  AttacherType = Attacher::AttachEngine3D
  Height = 7
  Length = 5
  Placement = pos=(-5,0,-2) rot=(0,0,1;0rad)
  Width = 40
FEATURE [Part::Box] Box291  label="Cube245"
  AttacherType = Attacher::AttachEngine3D
  Height = 7
  Length = 4
  Placement = pos=(-6,8,-2) rot=(0,0,1;0rad)
  Width = 2
FEATURE [Part::Box] Box292  label="Chamfer Cube010"
  AttacherType = Attacher::AttachEngine3D
  Height = 10
  Length = 13
  Placement = pos=(-11.69,0,-1.19) rot=(0,-1,0;0.785398rad)
  Width = 40
FEATURE [Part::Box] Box293  label="Cube246"
  AttacherType = Attacher::AttachEngine3D
  Height = 7
  Length = 10
  Placement = pos=(-15,6,-2) rot=(0,0,1;0rad)
  Width = 2
FEATURE [Part::Sphere] Sphere094
  Angle1 = -90
  Angle2 = 90
  Angle3 = 360
  AttacherType = Attacher::AttachEngine3D
  Placement = pos=(-7.5,11.5,0.5) rot=(0,0,1;0rad)
  Radius = 1.25
FEATURE [Part::Box] Box294  label="Cube247"
  AttacherType = Attacher::AttachEngine3D
  Height = 7
  Length = 4
  Placement = pos=(-6,27.4,-2) rot=(0,0,1;0rad)
  Width = 7.2
FEATURE [Part::Box] Box295  label="Cube248"
  AttacherType = Attacher::AttachEngine3D
  Height = 7
  Length = 4
  Placement = pos=(-6,12,-2) rot=(0,0,1;0rad)
  Width = 1
FEATURE [Part::Box] Box296  label="Cube249"
  AttacherType = Attacher::AttachEngine3D
  Height = 7
  Length = 4
  Placement = pos=(-6,24.4,-2) rot=(0,0,1;0rad)
  Width = 1
FEATURE [Part::Sphere] Sphere095
  Angle1 = -90
  Angle2 = 90
  Angle3 = 360
  AttacherType = Attacher::AttachEngine3D
  Placement = pos=(-7.5,6.5,0.5) rot=(0,0,1;0rad)
  Radius = 1.25
FEATURE [Part::Box] Box297  label="Cube250"
  AttacherType = Attacher::AttachEngine3D
  Height = 7
  Length = 4
  Placement = pos=(-6,36.6,-2) rot=(0,0,1;0rad)
  Width = 1
FEATURE [Part::Box] Box298  label="Cube251"
  AttacherType = Attacher::AttachEngine3D
  Height = 7
  Length = 10
  Placement = pos=(-15,10,-2) rot=(0,0,1;0rad)
  Width = 2
FEATURE [Part::Sphere] Sphere096
  Angle1 = -90
  Angle2 = 90
  Angle3 = 360
  AttacherType = Attacher::AttachEngine3D
  Placement = pos=(-7.5,34,0.5) rot=(0,0,1;0rad)
  Radius = 1.5
FEATURE [Part::Box] Box299  label="Cube252"
  AttacherType = Attacher::AttachEngine3D
  Height = 7
  Length = 4
  Placement = pos=(-6,5,-2) rot=(0,0,1;0rad)
  Width = 1
FEATURE [Part::MultiFuse] Fusion103019  label="Extra Holes for Clips010"
  Shapes = -> [Box294,Box295,Box297,Box291,Box296,Box299]
FEATURE [Part::Box] Box300  label="Re-level Edge Clip Block020"
  AttacherType = Attacher::AttachEngine3D
  Height = 10
  Length = 20
  Placement = pos=(-19,-2,3) rot=(0,0,1;0rad)
  Width = 44
FEATURE [Part::Box] Box301  label="Cube253"
  AttacherType = Attacher::AttachEngine3D
  Height = 7
  Length = 10
  Placement = pos=(-15,34.6,-2) rot=(0,0,1;0rad)
  Width = 2
FEATURE [Part::Box] Box302  label="Cube254"
  AttacherType = Attacher::AttachEngine3D
  Height = 7
  Length = 10
  Placement = pos=(-15,25.4,-2) rot=(0,0,1;0rad)
  Width = 2
FEATURE [Part::MultiFuse] Fusion103020
  Shapes = -> [Box290,Box293,Box298,Box302,Box301]
FEATURE [Part::Fuse] Fusion103021  label="Bumps010"
  Base = -> Sphere095
  Tool = -> Sphere094
FEATURE [Part::Fuse] Fusion103018
  Base = -> Fusion103021
  Tool = -> Fusion103020
FEATURE [Part::Sphere] Sphere097
  Angle1 = -90
  Angle2 = 90
  Angle3 = 360
  AttacherType = Attacher::AttachEngine3D
  Placement = pos=(-7.5,28,0.5) rot=(0,0,1;0rad)
  Radius = 1.5
FEATURE [Part::Fuse] Fusion103022  label="Holes010"
  Base = -> Sphere097
  Tool = -> Sphere096
FEATURE [Part::Box] Box303  label="Re-level Edge Clip Block021"
  AttacherType = Attacher::AttachEngine3D
  Height = 10
  Length = 12
  Placement = pos=(-21.5,-2,-7) rot=(0,0,1;0rad)
  Width = 44
FEATURE [Part::Cut] Cut122
  Base = -> Fusion103018
  Tool = -> Fusion103022
FEATURE [Part::Cut] Cut123
  Base = -> Cut122
  Tool = -> Fusion103019
FEATURE [Part::Cut] Cut124
  Base = -> Cut123
  Tool = -> Box300
FEATURE [Part::Cut] Cut125
  Base = -> Cut124
  Tool = -> Box303
FEATURE [Part::Cut] Cut126  label="Edge Clips007"
  Base = -> Cut125
  Placement = pos=(20,-20,0) rot=(0,0,1;1.5708rad)
  Tool = -> Box292
FEATURE [Part::Box] Box304  label="Re-level Edge Clip Block022"
  AttacherType = Attacher::AttachEngine3D
  Height = 10
  Length = 12
  Placement = pos=(-21.5,-2,-7) rot=(0,0,1;0rad)
  Width = 44
FEATURE [Part::Box] Box305  label="Cube255"
  AttacherType = Attacher::AttachEngine3D
  Height = 7
  Length = 4
  Placement = pos=(-6,36.6,-2) rot=(0,0,1;0rad)
  Width = 1
FEATURE [Part::Box] Box306  label="Cube256"
  AttacherType = Attacher::AttachEngine3D
  Height = 7
  Length = 10
  Placement = pos=(-15,10,-2) rot=(0,0,1;0rad)
  Width = 2
FEATURE [Part::Box] Box307  label="Cube257"
  AttacherType = Attacher::AttachEngine3D
  Height = 7
  Length = 10
  Placement = pos=(-15,25.4,-2) rot=(0,0,1;0rad)
  Width = 2
FEATURE [Part::Box] Box308  label="Re-level Edge Clip Block023"
  AttacherType = Attacher::AttachEngine3D
  Height = 10
  Length = 20
  Placement = pos=(-19,-2,3) rot=(0,0,1;0rad)
  Width = 44
FEATURE [Part::Box] Box309  label="Cube258"
  AttacherType = Attacher::AttachEngine3D
  Height = 7
  Length = 10
  Placement = pos=(-15,34.6,-2) rot=(0,0,1;0rad)
  Width = 2
FEATURE [Part::Sphere] Sphere098
  Angle1 = -90
  Angle2 = 90
  Angle3 = 360
  AttacherType = Attacher::AttachEngine3D
  Placement = pos=(-7.5,34,0.5) rot=(0,0,1;0rad)
  Radius = 1.5
FEATURE [Part::Sphere] Sphere099
  Angle1 = -90
  Angle2 = 90
  Angle3 = 360
  AttacherType = Attacher::AttachEngine3D
  Placement = pos=(-7.5,28,0.5) rot=(0,0,1;0rad)
  Radius = 1.5
FEATURE [Part::Fuse] Fusion103023  label="Holes011"
  Base = -> Sphere099
  Tool = -> Sphere098
FEATURE [Part::Box] Box310  label="Cube259"
  AttacherType = Attacher::AttachEngine3D
  Height = 7
  Length = 4
  Placement = pos=(-6,5,-2) rot=(0,0,1;0rad)
  Width = 1
FEATURE [Part::Box] Box311  label="Cube260"
  AttacherType = Attacher::AttachEngine3D
  Height = 7
  Length = 4
  Placement = pos=(-6,24.4,-2) rot=(0,0,1;0rad)
  Width = 1
FEATURE [Part::Sphere] Sphere100
  Angle1 = -90
  Angle2 = 90
  Angle3 = 360
  AttacherType = Attacher::AttachEngine3D
  Placement = pos=(-7.5,11.5,0.5) rot=(0,0,1;0rad)
  Radius = 1.25
FEATURE [Part::Box] Box312  label="Cube261"
  AttacherType = Attacher::AttachEngine3D
  Height = 7
  Length = 4
  Placement = pos=(-6,12,-2) rot=(0,0,1;0rad)
  Width = 1
FEATURE [Part::Box] Box313  label="Chamfer Cube011"
  AttacherType = Attacher::AttachEngine3D
  Height = 10
  Length = 13
  Placement = pos=(-11.69,0,-1.19) rot=(0,-1,0;0.785398rad)
  Width = 40
FEATURE [Part::Sphere] Sphere101
  Angle1 = -90
  Angle2 = 90
  Angle3 = 360
  AttacherType = Attacher::AttachEngine3D
  Placement = pos=(-7.5,6.5,0.5) rot=(0,0,1;0rad)
  Radius = 1.25
FEATURE [Part::Fuse] Fusion103024  label="Bumps011"
  Base = -> Sphere101
  Tool = -> Sphere100
FEATURE [Part::Box] Box314  label="Cube262"
  AttacherType = Attacher::AttachEngine3D
  Height = 7
  Length = 5
  Placement = pos=(-5,0,-2) rot=(0,0,1;0rad)
  Width = 40
FEATURE [Part::Box] Box315  label="Cube263"
  AttacherType = Attacher::AttachEngine3D
  Height = 7
  Length = 4
  Placement = pos=(-6,27.4,-2) rot=(0,0,1;0rad)
  Width = 7.2
FEATURE [Part::Box] Box316  label="Cube264"
  AttacherType = Attacher::AttachEngine3D
  Height = 7
  Length = 4
  Placement = pos=(-6,8,-2) rot=(0,0,1;0rad)
  Width = 2
FEATURE [Part::MultiFuse] Fusion103025  label="Extra Holes for Clips011"
  Shapes = -> [Box315,Box312,Box305,Box316,Box311,Box310]
FEATURE [Part::Box] Box317  label="Cube265"
  AttacherType = Attacher::AttachEngine3D
  Height = 7
  Length = 10
  Placement = pos=(-15,6,-2) rot=(0,0,1;0rad)
  Width = 2
FEATURE [Part::MultiFuse] Fusion103026
  Shapes = -> [Box314,Box317,Box306,Box307,Box309]
FEATURE [Part::Fuse] Fusion103027
  Base = -> Fusion103024
  Tool = -> Fusion103026
FEATURE [Part::Cut] Cut128
  Base = -> Fusion103027
  Tool = -> Fusion103023
FEATURE [Part::Cut] Cut114
  Base = -> Cut128
  Tool = -> Fusion103025
FEATURE [Part::Cut] Cut129
  Base = -> Cut114
  Tool = -> Box308
FEATURE [Part::Cut] Cut115
  Base = -> Cut129
  Tool = -> Box304
FEATURE [Part::Cut] Cut127  label="Edge Clips008"
  Base = -> Cut115
  Placement = pos=(20,20,0) rot=(0,0,1;3.14159rad)
  Tool = -> Box313
FEATURE [Part::Box] Box318  label="Re-level Edge Clip Block024"
  AttacherType = Attacher::AttachEngine3D
  Height = 10
  Length = 12
  Placement = pos=(-21.5,-2,-7) rot=(0,0,1;0rad)
  Width = 44
FEATURE [Part::Box] Box319  label="Cube266"
  AttacherType = Attacher::AttachEngine3D
  Height = 7
  Length = 10
  Placement = pos=(-15,10,-2) rot=(0,0,1;0rad)
  Width = 2
FEATURE [Part::Box] Box320  label="Cube267"
  AttacherType = Attacher::AttachEngine3D
  Height = 7
  Length = 4
  Placement = pos=(-6,12,-2) rot=(0,0,1;0rad)
  Width = 1
FEATURE [Part::Box] Box321  label="Chamfer Cube012"
  AttacherType = Attacher::AttachEngine3D
  Height = 10
  Length = 13
  Placement = pos=(-11.69,0,-1.19) rot=(0,-1,0;0.785398rad)
  Width = 40
FEATURE [Part::Sphere] Sphere102
  Angle1 = -90
  Angle2 = 90
  Angle3 = 360
  AttacherType = Attacher::AttachEngine3D
  Placement = pos=(-7.5,6.5,0.5) rot=(0,0,1;0rad)
  Radius = 1.25
FEATURE [Part::Box] Box322  label="Cube268"
  AttacherType = Attacher::AttachEngine3D
  Height = 7
  Length = 5
  Placement = pos=(-5,0,-2) rot=(0,0,1;0rad)
  Width = 40
FEATURE [Part::Box] Box323  label="Cube269"
  AttacherType = Attacher::AttachEngine3D
  Height = 7
  Length = 4
  Placement = pos=(-6,27.4,-2) rot=(0,0,1;0rad)
  Width = 7.2
FEATURE [Part::Box] Box324  label="Cube270"
  AttacherType = Attacher::AttachEngine3D
  Height = 7
  Length = 4
  Placement = pos=(-6,8,-2) rot=(0,0,1;0rad)
  Width = 2
FEATURE [Part::Box] Box325  label="Cube271"
  AttacherType = Attacher::AttachEngine3D
  Height = 7
  Length = 10
  Placement = pos=(-15,6,-2) rot=(0,0,1;0rad)
  Width = 2
FEATURE [Part::Sphere] Sphere103
  Angle1 = -90
  Angle2 = 90
  Angle3 = 360
  AttacherType = Attacher::AttachEngine3D
  Placement = pos=(-7.5,28,0.5) rot=(0,0,1;0rad)
  Radius = 1.5
FEATURE [Part::Box] Box326  label="Cube272"
  AttacherType = Attacher::AttachEngine3D
  Height = 7
  Length = 4
  Placement = pos=(-6,5,-2) rot=(0,0,1;0rad)
  Width = 1
FEATURE [Part::Box] Box327  label="Cube273"
  AttacherType = Attacher::AttachEngine3D
  Height = 7
  Length = 4
  Placement = pos=(-6,24.4,-2) rot=(0,0,1;0rad)
  Width = 1
FEATURE [Part::Sphere] Sphere104
  Angle1 = -90
  Angle2 = 90
  Angle3 = 360
  AttacherType = Attacher::AttachEngine3D
  Placement = pos=(-7.5,11.5,0.5) rot=(0,0,1;0rad)
  Radius = 1.25
FEATURE [Part::Box] Box328  label="Re-level Edge Clip Block025"
  AttacherType = Attacher::AttachEngine3D
  Height = 10
  Length = 20
  Placement = pos=(-19,-2,3) rot=(0,0,1;0rad)
  Width = 44
FEATURE [Part::Box] Box329  label="Cube274"
  AttacherType = Attacher::AttachEngine3D
  Height = 7
  Length = 10
  Placement = pos=(-15,34.6,-2) rot=(0,0,1;0rad)
  Width = 2
FEATURE [Part::Box] Box330  label="Cube275"
  AttacherType = Attacher::AttachEngine3D
  Height = 7
  Length = 10
  Placement = pos=(-15,25.4,-2) rot=(0,0,1;0rad)
  Width = 2
FEATURE [Part::MultiFuse] Fusion103030
  Shapes = -> [Box322,Box325,Box319,Box330,Box329]
FEATURE [Part::Box] Box331  label="Cube276"
  AttacherType = Attacher::AttachEngine3D
  Height = 7
  Length = 4
  Placement = pos=(-6,36.6,-2) rot=(0,0,1;0rad)
  Width = 1
FEATURE [Part::MultiFuse] Fusion103029  label="Extra Holes for Clips012"
  Shapes = -> [Box323,Box320,Box331,Box324,Box327,Box326]
FEATURE [Part::Fuse] Fusion103032  label="Bumps012"
  Base = -> Sphere102
  Tool = -> Sphere104
FEATURE [Part::Fuse] Fusion103028
  Base = -> Fusion103032
  Tool = -> Fusion103030
FEATURE [Part::Sphere] Sphere105
  Angle1 = -90
  Angle2 = 90
  Angle3 = 360
  AttacherType = Attacher::AttachEngine3D
  Placement = pos=(-7.5,34,0.5) rot=(0,0,1;0rad)
  Radius = 1.5
FEATURE [Part::Fuse] Fusion103031  label="Holes012"
  Base = -> Sphere103
  Tool = -> Sphere105
FEATURE [Part::Cut] Cut134
  Base = -> Fusion103028
  Tool = -> Fusion103031
FEATURE [Part::Cut] Cut130
  Base = -> Cut134
  Tool = -> Fusion103029
FEATURE [Part::Cut] Cut131
  Base = -> Cut130
  Tool = -> Box328
FEATURE [Part::Cut] Cut132
  Base = -> Cut131
  Tool = -> Box318
FEATURE [Part::Cut] Cut133  label="Edge Clips009"
  Base = -> Cut132
  Placement = pos=(-20,20,0) rot=(0,0,-1;1.5708rad)
  Tool = -> Box321
FEATURE [Part::Box] Box332  label="Cube277"
  AttacherType = Attacher::AttachEngine3D
  Height = 10
  Length = 10
  Placement = pos=(4,-26,1) rot=(0.205904,-0.974848,-0.085288;0.803573rad)
  Width = 15
FEATURE [Part::Box] Box333  label="Cube278"
  AttacherType = Attacher::AttachEngine3D
  Height = 10
  Length = 10
  Placement = pos=(-26,-4,1) rot=(-0.273007,-0.419215,-0.865867;1.78566rad)
  Width = 15
FEATURE [Part::Box] Box334  label="Cube279"
  AttacherType = Attacher::AttachEngine3D
  Height = 10
  Length = 10
  Placement = pos=(-4,26,1) rot=(0.381439,0.080566,0.920876;3.07487rad)
  Width = 15
FEATURE [Part::Box] Box335  label="Cube280"
  AttacherType = Attacher::AttachEngine3D
  Height = 10
  Length = 10
  Placement = pos=(26,4,1) rot=(0.442189,-0.287968,0.849437;1.66134rad)
  Width = 15
FEATURE [Part::MultiFuse] Fusion103033  label="Glue Dents002"
  Shapes = -> [Box332,Box333,Box334,Box335]
FEATURE [Part::MultiFuse] Fusion103034  label="Edge Clips Fusion002"
  Shapes = -> [Cut133,Cut121,Cut126,Cut127]
FEATURE [Part::MultiFuse] Fusion103035
  Placement = pos=(-15,-15,0) rot=(0,0,1;0rad)
  Shapes = -> [Box270,Cylinder042,Sphere089]
FEATURE [Part::Box] Box336  label="Square Nut Hole 026"
  AttacherType = Attacher::AttachEngine3D
  Height = 2
  Length = 5.8
  Placement = pos=(-2.9,2.9,2.1) rot=(1,0,0;3.14159rad)
  Width = 5.8
FEATURE [Part::Cylinder] Cylinder043
  Angle = 360
  AttacherType = Attacher::AttachEngine3D
  Height = 10
  Placement = pos=(0,0,6.7) rot=(1,0,0;3.14159rad)
  Radius = 1.7
FEATURE [Part::Sphere] Sphere106
  Angle1 = -90
  Angle2 = 90
  Angle3 = 360
  AttacherType = Attacher::AttachEngine3D
  Placement = pos=(0,0,4.3) rot=(1,0,0;3.14159rad)
  Radius = 3.35
FEATURE [Part::MultiFuse] Fusion103036
  Placement = pos=(-15,0,0) rot=(0,0,1;0rad)
  Shapes = -> [Box336,Cylinder043,Sphere106]
FEATURE [Part::Fuse] Fusion103037
  Base = -> Fusion103035
  Tool = -> Fusion103036
FEATURE [Part::MultiFuse] Fusion103038  label="Nut Holes001"
  Shapes = -> [Fusion103037,Fusion103012,Fusion103011,Fusion103010]
FEATURE [Part::Fuse] Fusion103039  label="Cube with Edge Clips001"
  Base = -> Box271
  Tool = -> Fusion103034
FEATURE [Part::Cut] Cut135
  Base = -> Fusion103039
  Tool = -> Fusion103033
FEATURE [Part::Cut] Cut136
  Base = -> Cut135
  Tool = -> Fusion103038
FEATURE [Part::Cut] Cut137
  Base = -> Cut136
  Tool = -> Chamfer016
FEATURE [Part::Cut] Cut138
  Base = -> Cut137
  Tool = -> Chamfer015
FEATURE [Part::Cut] Cut139  label="Nut Plate 1.003"
  Base = -> Cut138
  Tool = -> Box272
FEATURE [Part::Cylinder] Cylinder044
  Angle = 360
  AttacherType = Attacher::AttachEngine3D
  Height = 4
  Placement = pos=(-9.75,-9.75,-3) rot=(0,0,1;0rad)
  Radius = 1.5
FEATURE [Part::Cylinder] Cylinder045
  Angle = 360
  AttacherType = Attacher::AttachEngine3D
  Height = 4
  Placement = pos=(9.75,-9.75,-3) rot=(0,0,1;0rad)
  Radius = 1.5
FEATURE [Part::Cylinder] Cylinder046
  Angle = 360
  AttacherType = Attacher::AttachEngine3D
  Height = 4
  Placement = pos=(-9.75,9.75,-3) rot=(0,0,1;0rad)
  Radius = 1.5
FEATURE [Part::Cylinder] Cylinder047
  Angle = 360
  AttacherType = Attacher::AttachEngine3D
  Height = 4
  Placement = pos=(9.75,9.75,-3) rot=(0,0,1;0rad)
  Radius = 1.5
FEATURE [Part::MultiFuse] Fusion103040
  Shapes = -> [Cylinder044,Cylinder047,Cylinder045,Cylinder046]
FEATURE [Part::Cut] Cut140  label="Nut Plate 1.004"
  Base = -> Cut139
  Placement = pos=(0,0,-6) rot=(0,0,1;0rad)
  Tool = -> Fusion103040
FEATURE [App::DocumentObjectGroup] Group003  label="Cube-components"
  Group = -> [Cut112,Cut113]
FEATURE [Part::Box] Box404  label="Cube334"
  AttacherType = Attacher::AttachEngine3D
  Height = 14
  Length = 5
  Placement = pos=(20,20,-7) rot=(0,0,1;0rad)
  Width = 5
FEATURE [Part::Box] Box405  label="Cube335"
  AttacherType = Attacher::AttachEngine3D
  Height = 13
  Length = 15
  Placement = pos=(10,10,2) rot=(0,0,1;0rad)
  Width = 15
FEATURE [Part::FeaturePython] BevelGear001  # WARN: FeaturePython — macro-defined, semantics opaque (R4)
  Placement = pos=(7.81,7.81,10.5) rot=(0.862856,-0.357407,-0.357407;1.71777rad)
  backlash = 0
  beta = 0
  clearance = 0.1
  height = 3
  m = 1
  numpoints = 6
  pitch_angle = 45
  pressure_angle = 20
  reset_origin = true
  teeth = 10
FEATURE [Part::Cylinder] Cylinder054
  Angle = 360
  AttacherType = Attacher::AttachEngine3D
  Height = 22
  Radius = 11
FEATURE [Part::Cone] Cone
  Angle = 360
  AttacherType = Attacher::AttachEngine3D
  Height = 9
  Placement = pos=(8.52,8.52,10.5) rot=(0.862856,-0.357407,-0.357407;1.71777rad)
  Radius1 = 8
  Radius2 = 1.5
FEATURE [Part::Box] Box406004  label="Square Nut Hole 029"
  AttacherType = Attacher::AttachEngine3D
  Height = 2
  Length = 5.8
  Placement = pos=(15.7,19.8,7.6) rot=(0.862856,-0.357407,-0.357407;1.71777rad)
  Width = 14.8
FEATURE [Part::Box] Box406005  label="60mm-high"
  AttacherType = Attacher::AttachEngine3D
  Height = 60
  Length = 10
  Placement = pos=(-29,12,-3) rot=(0,0,1;0rad)
  Width = 10
FEATURE [Part::Cylinder] Cylinder057  label="small-gear-hub"
  Angle = 360
  AttacherType = Attacher::AttachEngine3D
  Height = 5
  Placement = pos=(7.5,7.5,10.5) rot=(0.862856,-0.357407,-0.357407;1.71777rad)
  Radius = 4
FEATURE [Part::Feature] Shape001  label="M3-hex-cavity"
  Placement = pos=(-0.5,-0.5,10.5) rot=(0.281085,0.678598,0.678598;2.59356rad)
  shape: bbox 11.56 x 11.56 x 5.5 mm, 8 faces (baked)
FEATURE [Part::Cylinder] Cylinder058  label="M3-screw-drive001"
  Angle = 360
  AttacherType = Attacher::AttachEngine3D
  Height = 33
  Placement = pos=(23.37,23.37,10.5) rot=(0.862856,-0.357407,-0.357407;1.71777rad)
  Radius = 1.75
FEATURE [Part::Box] Box406007  label="Cube338"
  AttacherType = Attacher::AttachEngine3D
  Height = 14
  Length = 14
  Placement = pos=(1.78,11.68,2) rot=(0,0,-1;0.785398rad)
  Width = 10
FEATURE [Part::Box] Box406008  label="slot-1"
  AttacherType = Attacher::AttachEngine3D
  Height = 36
  Length = 10.5
  Placement = pos=(10.22,17.65,0) rot=(0,0,-1;0.785398rad)
  Width = 28
FEATURE [Part::Cylinder] Cylinder059  label="M3-screw-drive002"
  Angle = 360
  AttacherType = Attacher::AttachEngine3D
  Height = 80
  Placement = pos=(26.8701,26.8701,10.5) rot=(0.862856,-0.357407,-0.357407;1.71777rad)
  Radius = 2.15
FEATURE [Part::Cylinder] Cylinder066  label="M3-screw-drive003"
  Angle = 360
  AttacherType = Attacher::AttachEngine3D
  Height = 33
  Placement = pos=(26.8701,26.8701,10.5) rot=(0.862856,-0.357407,-0.357407;1.71777rad)
  Radius = 1.75
FEATURE [Part::MultiFuse] Fusion103077010  label="finger-cavity"
  Shapes = -> [Cylinder066,Box406004]
FEATURE [Part::Box] Box406015  label="motor-clamp-0"
  AttacherType = Attacher::AttachEngine3D
  Height = 31
  Length = 53.28
  Placement = pos=(-13.8876,-23.7871,2) rot=(0,0,1;0.785398rad)
  Width = 14
FEATURE [Part::Box] Box406016  label="clamp-slot"
  AttacherType = Attacher::AttachEngine3D
  Height = 21
  Length = 49
  Placement = pos=(-15.9,-17.31,17) rot=(0,0,1;0.785398rad)
  Width = 2
FEATURE [Part::Cylinder] Cylinder067
  Angle = 360
  AttacherType = Attacher::AttachEngine3D
  Height = 15
  Placement = pos=(0,0,9) rot=(0,0,1;0rad)
  Radius = 6.25
FEATURE [Part::Box] Box406017  label="gearbox001"
  AttacherType = Attacher::AttachEngine3D
  Height = 27
  Length = 16
  Placement = pos=(-8,-5.25,0) rot=(0,0,1;0rad)
  Width = 10.5
FEATURE [Part::MultiCommon] Common004  label="motor-hole"
  Placement = pos=(0,0,11) rot=(0,0,-1;0.785398rad)
  Shapes = -> [Cylinder067,Box406017]
FEATURE [Part::Cylinder] Cylinder068
  Angle = 360
  AttacherType = Attacher::AttachEngine3D
  Height = 12
  Radius = 1.2
FEATURE [Part::Cylinder] Cylinder069
  Angle = 360
  AttacherType = Attacher::AttachEngine3D
  Height = 12
  Placement = pos=(0,0,12) rot=(0,0,1;0rad)
  Radius = 2.2
FEATURE [Part::MultiFuse] Fusion103077013  label="M2-screw001"
  Placement = pos=(0,13,30) rot=(0.862856,0.357407,0.357407;1.71777rad)
  Shapes = -> [Cylinder068,Cylinder069]
FEATURE [Part::Feature] Fusion103077013001
  Placement = pos=(-2e-15,-13,30) rot=(-0.281085,0.678598,0.678598;3.68962rad)
  shape: bbox 19.37 x 19.37 x 4.4 mm, 5 faces (baked)
FEATURE [Part::MultiFuse] Fusion103077013002  label="motor-clamp-screws"
  Shapes = -> [Fusion103077013,Fusion103077013001]
FEATURE [Part::Cylinder] Cylinder070
  Angle = 360
  AttacherType = Attacher::AttachEngine3D
  Height = 12
  Placement = pos=(0,0,12) rot=(0,0,1;0rad)
  Radius = 2.2
FEATURE [Part::Cylinder] Cylinder071
  Angle = 360
  AttacherType = Attacher::AttachEngine3D
  Height = 12
  Radius = 1.2
FEATURE [Part::Cylinder] Cylinder072  label="M3-cap-screw-head"
  Angle = 360
  AttacherType = Attacher::AttachEngine3D
  Height = 10
  Placement = pos=(0,15,4) rot=(0,0,1;0rad)
  Radius = 3
FEATURE [Part::FeaturePython] BevelGear002  # WARN: FeaturePython — macro-defined, semantics opaque (R4)
  Placement = pos=(0,0,2.5) rot=(0,0,1;0rad)
  backlash = 0
  beta = 0
  clearance = 0.1
  height = 3
  m = 1
  numpoints = 6
  pitch_angle = 45
  pressure_angle = 20
  reset_origin = true
  teeth = 20
FEATURE [Part::MultiCommon] Common  label="big-gear-a"
  Shapes = -> [BevelGear002,Cylinder054]
FEATURE [Part::MultiCommon] Common005  label="small-gear-1"
  Shapes = -> [Cone,BevelGear001]
FEATURE [Part::MultiFuse] Fusion103077013004005  label="small-gear-2"
  Shapes = -> [Common005,Cylinder057]
FEATURE [Part::MultiFuse] Fusion103077013004006  label="small-gear-cavity"
  Shapes = -> [Cylinder058,Shape001]
FEATURE [Part::Cut] Cut173011005  label="small-gear"
  Base = -> Fusion103077013004005
  Tool = -> Fusion103077013004006
FEATURE [Part::Cylinder] Cylinder073  label="motor-bulge"
  Angle = 360
  AttacherType = Attacher::AttachEngine3D
  Height = 10
  Placement = pos=(0,0,23) rot=(0,0,1;0rad)
  Radius = 9
FEATURE [Part::Cylinder] Cylinder074  label="big-gear-clearance"
  Angle = 360
  AttacherType = Attacher::AttachEngine3D
  Height = 22
  Radius = 12
FEATURE [Part::MultiFuse] Fusion103077013004008  label="motor-clamp-holes-1"
  Shapes = -> [Common004,Fusion103077013002,Box406016]
FEATURE [Part::Cylinder] Cylinder075  label="M3-cap-screw-head001"
  Angle = 360
  AttacherType = Attacher::AttachEngine3D
  Height = 10
  Placement = pos=(0,15,-6) rot=(0,0,1;0rad)
  Radius = 1.7
FEATURE [Part::MultiFuse] Fusion103077013004011  label="M3-cap-screw"
  Placement = pos=(0,0,5) rot=(0,0,1;0rad)
  Shapes = -> [Cylinder075,Cylinder072]
FEATURE [Part::Box] Box406019  label="motor-clamp-print-45"
  AttacherType = Attacher::AttachEngine3D
  Height = 30
  Length = 16.46
  Placement = pos=(-19.23,2.77,20) rot=(0.707107,0.707107,0;1.5708rad)
  Width = 16.46
FEATURE [Part::Feature] Box406008001  label="slot-2"
  Placement = pos=(-10.22,-17.65,0) rot=(0,0,1;2.35619rad)
  shape: bbox 27.22 x 27.22 x 36 mm, 6 faces (baked)
FEATURE [Part::Box] Box406008002  label="Cube339"
  AttacherType = Attacher::AttachEngine3D
  Height = 20
  Length = 23
  Placement = pos=(-1.06066,-15.2028,0) rot=(0,0,1;0.785398rad)
  Width = 20
FEATURE [Part::Fillet] Fillet001
  Base = -> Box406019
  Edges = 1 edges r=3: [Edge3]
FEATURE [Part::MultiFuse] Fusion103077013004012  label="mount-central-hole"
  Shapes = -> [Box406008002,Fillet001]
FEATURE [Part::MultiFuse] Fusion103077013004013  label="finger-slots"
  Shapes = -> [Box406008,Box406008001]
FEATURE [Part::Chamfer] Chamfer024  label="motor-clamp-1"
  Base = -> Box406015
  Edges = 2 edges r=12: [Edge2,Edge6]
FEATURE [Part::MultiFuse] Fusion103077013004014  label="motor-clamp-holes-2"
  Shapes = -> [Fusion103077013004008,Fusion103077013004012]
FEATURE [Part::Chamfer] Chamfer025  label="motor-clamp-2"
  Base = -> Chamfer024
  Edges = 4 edges r=2: [Edge1,Edge4,Edge5,Edge14]
FEATURE [Part::MultiFuse] Fusion103077013004015  label="motor-clamp-holes-3"
  Shapes = -> [Fusion103077013004014,Fusion103077013004013]
FEATURE [Part::MultiFuse] Fusion103077013004016  label="motor-clamp-3"
  Shapes = -> [Chamfer025,Cylinder073]
FEATURE [Part::Cut] Cut173011006  label="motor-clamp-4"
  Base = -> Fusion103077013004016
  Tool = -> Fusion103077013004015
FEATURE [Part::Fillet] Fillet002  label="motor-clamp-5"
  Base = -> Cut173011006
  Edges = 4 edges r=0.7: [Edge102,Edge119,Edge142,Edge146]
FEATURE [Part::Box] Box406008003  label="Cube340"
  AttacherType = Attacher::AttachEngine3D
  Height = 6
  Length = 15
  Placement = pos=(-5,10,2) rot=(0,0,1;0rad)
  Width = 10
FEATURE [Part::Cut] Cut173011007  label="screw-land-1"
  Base = -> Box406008003
  Tool = -> Cylinder074
FEATURE [Part::Cone] Cone001
  Angle = 360
  AttacherType = Attacher::AttachEngine3D
  Height = 9
  Placement = pos=(8.52,8.52,10.5) rot=(0.862856,-0.357407,-0.357407;1.71777rad)
  Radius1 = 9
  Radius2 = 2.5
FEATURE [Part::Cut] Cut173011008  label="Screw-land-2"
  Base = -> Cut173011007
  Tool = -> Cone001
FEATURE [Part::Cut] Cut173011009  label="screw-land-3"
  Base = -> Cut173011008
  Tool = -> Fusion103077013004011
FEATURE [Part::Fillet] Fillet003
  Base = -> Cut173011009
  Edges = 1 edges r=4: [Edge4]
FEATURE [Part::Fillet] Fillet004  label="screw-land-4"
  Base = -> Fillet003
  Edges = 1 edges r=3: [Edge3]
FEATURE [Part::Fillet] Fillet005  label="screw-land-005"
  Base = -> Fillet003
  Edges = 1 edges r=3: [Edge3]
FEATURE [Part::Mirroring] Part__Mirroring002  label="screw-land-005 (Mirror #3)"
  Base = (0,0,0)
  Normal = (1,0,0)
  Placement = pos=(0,0,0) rot=(0,0,1;1.5708rad)
  Source = -> Fillet005
FEATURE [Part::MultiFuse] Fusion103077013004017  label="screw-lands-1"
  Shapes = -> [Fillet004,Part__Mirroring002]
FEATURE [Part::Feature] Fusion103077013004017001  label="screw-lands-2"
  Placement = pos=(0,0,0) rot=(0,0,1;3.14159rad)
  shape: bbox 30 x 30 x 6.628 mm, 26 faces, 2 solids (baked)
FEATURE [Part::MultiFuse] Fusion103077013004017002  label="screw-lands"
  Shapes = -> [Fusion103077013004017001,Fusion103077013004017]
FEATURE [Part::MultiFuse] Fusion103077013004017003  label="motor-clamp-6"
  Shapes = -> [Fillet002,Fusion103077013004017002]
FEATURE [Part::Cut] Cut173011010  label="motor-clamp"
  Base = -> Fusion103077013004017003
  Tool = -> Cylinder059
FEATURE [Part::Box] Box406008004  label="gearbox004"
  AttacherType = Attacher::AttachEngine3D
  Height = 9
  Length = 12
  Placement = pos=(-6,-5,0) rot=(0,0,1;0rad)
  Width = 10
FEATURE [Part::Cylinder] Cylinder076  label="boss002"
  Angle = 360
  AttacherType = Attacher::AttachEngine3D
  Height = 1
  Placement = pos=(0,0,-1) rot=(0,0,1;0rad)
  Radius = 2
FEATURE [Part::Cylinder] Cylinder077
  Angle = 360
  AttacherType = Attacher::AttachEngine3D
  Height = 15
  Placement = pos=(0,0,9) rot=(0,0,1;0rad)
  Radius = 6
FEATURE [Part::Box] Box406008005  label="gearbox005"
  AttacherType = Attacher::AttachEngine3D
  Height = 27
  Length = 16
  Placement = pos=(-8,-5,0) rot=(0,0,1;0rad)
  Width = 10
FEATURE [Part::MultiCommon] Common001  label="motor002"
  Shapes = -> [Cylinder077,Box406008005]
FEATURE [Part::Cylinder] Cylinder078  label="shaft-002"
  Angle = 360
  AttacherType = Attacher::AttachEngine3D
  Height = 10
  Placement = pos=(0,0,-10) rot=(0,0,1;0rad)
  Radius = 1.5
FEATURE [Part::Box] Box406008006  label="Cube341"
  AttacherType = Attacher::AttachEngine3D
  Height = 12
  Length = 10
  Placement = pos=(-5,1,-11) rot=(0,0,1;0rad)
  Width = 10
FEATURE [Part::Cut] Cut001  label="shaft002"
  Base = -> Cylinder078
  Tool = -> Box406008006
FEATURE [Part::MultiFuse] Fusion103077013004017004  label="motor-assembled"
  Placement = pos=(0,0,11) rot=(0,0,-1;0.785398rad)
  Shapes = -> [Box406008004,Cylinder076,Common001,Cut001]
FEATURE [Part::Cylinder] Cylinder079  label="shaft-003"
  Angle = 360
  AttacherType = Attacher::AttachEngine3D
  Height = 10
  Placement = pos=(0,0,-2) rot=(0,0,1;0rad)
  Radius = 1.75
FEATURE [Part::Box] Box406008007  label="Cube342"
  AttacherType = Attacher::AttachEngine3D
  Height = 12
  Length = 10
  Placement = pos=(-5,1.125,-2) rot=(0,0,1;0rad)
  Width = 10
FEATURE [Part::Cut] Cut173011011  label="motor-shaft"
  Base = -> Cylinder079
  Tool = -> Box406008007
FEATURE [Part::Cut] Cut173011012  label="big-gear-2"
  Base = -> Common
  Tool = -> Cut173011011
FEATURE [Part::Box] Box406008008  label="Cube343"
  AttacherType = Attacher::AttachEngine3D
  Height = 2
  Length = 19
  Placement = pos=(-9.5,-9.5,0) rot=(0,0,1;0rad)
  Width = 19
FEATURE [Part::Cylinder] Cylinder080  label="Cylinder078"
  Angle = 360
  AttacherType = Attacher::AttachEngine3D
  Height = 10
  Placement = pos=(0,0,-4) rot=(0,0,1;0rad)
  Radius = 1.8
FEATURE [Part::Cut] Cut173011013  label="filler-plate-1"
  Base = -> Box406008008
  Tool = -> Cylinder080
FEATURE [Part::Chamfer] Chamfer026  label="filler-plate-2"
  Base = -> Cut173011013
  Edges = 1 edges r=0.5: [Edge10]
FEATURE [Part::Chamfer] Chamfer027  label="filler-plate"
  Base = -> Chamfer026
  Edges = 4 edges r=0.5: [Edge10,Edge11,Edge13,Edge15]
FEATURE [Part::Box] Box406008009  label="Cube344"
  AttacherType = Attacher::AttachEngine3D
  Height = 3
  Length = 6
  Placement = pos=(19,19,-7) rot=(0,0,1;0rad)
  Width = 6
FEATURE [Part::Chamfer] Chamfer029  label="grip-1"
  Base = -> Box406008009
  Edges = 2 edges r=1: [Edge2,Edge10]
FEATURE [Part::Chamfer] Chamfer030  label="grip-2"
  Base = -> Chamfer029
  Edges = 1 edges r=1: [Edge1]
FEATURE [Part::Cut] Cut173011016  label="mounting-plate"
  Base = -> Cut139
  Placement = pos=(0,0,0) rot=(1,0,0;3.14159rad)
  Tool = -> Fusion103040
FEATURE [Part::Chamfer] Chamfer032  label="big-gear"
  Base = -> Cut173011012
  Edges = 3 edges r=0.5: [Edge124,Edge125,Edge126]
FEATURE [Part::Feature] Shape002  label="M3-head-cover"
  Placement = pos=(5,5,10.5) rot=(0.862856,-0.357407,-0.357407;1.71777rad)
  shape: bbox 5.347 x 5.347 x 5.25 mm, 8 faces (baked)
FEATURE [Part::Cylinder] Cylinder081  label="M3-screw-drive004"
  Angle = 360
  AttacherType = Attacher::AttachEngine3D
  Height = 20
  Placement = pos=(23.4,23.4,10.5) rot=(0.862856,-0.357407,-0.357407;1.71777rad)
  Radius = 4.5
FEATURE [Part::Feature] Cylinder081001
  Placement = pos=(-23.4,-23.4,10.5) rot=(0.281085,0.678598,0.678598;2.59356rad)
  shape: bbox 20.51 x 20.51 x 9 mm, 3 faces (baked)
FEATURE [Part::MultiFuse] Fusion103077013004017006  label="nut-cavities"
  Shapes = -> [Cylinder081001,Cylinder081]
FEATURE [App::DocumentObjectGroup] Group001  label="Old"
  Group = -> [Cut008,Cut009,Cut015,Cut018,Fusion021,Fusion023,Group,Cut039,Cut028,Cut032,Cut033,Fusion048,Cylinder068,Cylinder069,Cylinder071,Cylinder070,Fusion103077013004017006]
FEATURE [Part::Chamfer] Chamfer  label="finger-1"
  Base = -> Box405
  Edges = 2 edges r=8.5: [Edge3,Edge5]
FEATURE [Part::Cut] Cut173011017  label="finger-2"
  Base = -> Chamfer
  Tool = -> Box406007
FEATURE [Part::Fillet] Fillet  label="finger-3"
  Base = -> Cut173011017
  Edges = 2 edges r=1.5: [Edge8,Edge14]
FEATURE [Part::Chamfer] Chamfer033  label="grip-3"
  Base = -> Chamfer030
  Edges = 3 edges r=1: [Edge4,Edge10,Edge15]
FEATURE [Part::MultiFuse] Fusion103077013004017007  label="finger-4"
  Shapes = -> [Chamfer033,Box404,Fillet]
FEATURE [Part::Fillet] Fillet006  label="finger-5"
  Base = -> Fusion103077013004017007
  Edges = 4 edges r=3: [Edge33,Edge41,Edge51,Edge59]
FEATURE [Part::Cut] Cut173011018  label="finger-6"
  Base = -> Fillet006
  Tool = -> Fusion103077010
FEATURE [Part::Chamfer] Chamfer034  label="finger"
  Base = -> Cut173011018
  Edges = 4 edges r=0.7: [Edge81,Edge82,Edge83,Edge84]
FEATURE [Part::Box] Box406008010  label="Cube345"
  AttacherType = Attacher::AttachEngine3D
  Height = 5
  Length = 10
  Placement = pos=(4,5,0.8) rot=(0,0,1;0.785398rad)
  Width = 1
FEATURE [Part::Box] Box406008011  label="Cube346"
  AttacherType = Attacher::AttachEngine3D
  Height = 5
  Length = 10
  Placement = pos=(7.3,5,0.8) rot=(0,0,1;0.785398rad)
  Width = 1
FEATURE [Part::Fuse] Fusion103077013004017008
  Base = -> Box406008010
  Tool = -> Box406008011
FEATURE [Part::Feature] Fusion103077013004017008001
  Placement = pos=(-4.36408,4.36408,2.00532) rot=(0.707107,0.707107,0;0.628319rad)
  shape: bbox 12.71 x 10.04 x 6.004 mm, 12 faces, 2 solids (baked)
FEATURE [Part::Feature] Fusion103077013004017008002
  Placement = pos=(-7.06123,7.06123,7.25532) rot=(0.707107,0.707107,0;1.25664rad)
  shape: bbox 12.81 x 11.79 x 4.715 mm, 12 faces, 2 solids (baked)
FEATURE [Part::Feature] Fusion103077013004017008003
  Placement = pos=(-7.06123,7.06123,13.7447) rot=(0.707107,0.707107,0;1.88496rad)
  shape: bbox 11.79 x 12.81 x 4.715 mm, 12 faces, 2 solids (baked)
FEATURE [Part::Feature] Fusion103077013004017008004
  Placement = pos=(-4.36408,4.36408,18.9947) rot=(0.707107,0.707107,0;2.51327rad)
  shape: bbox 10.04 x 12.71 x 6.004 mm, 12 faces, 2 solids (baked)
FEATURE [Part::Feature] Fusion103077013004017008005
  Placement = pos=(-9e-16,9e-16,21) rot=(0.707107,0.707107,0;3.14159rad)
  shape: bbox 7.778 x 11.08 x 5 mm, 12 faces, 2 solids (baked)
FEATURE [Part::Feature] Fusion103077013004017008006
  Placement = pos=(4.36408,-4.36408,18.9947) rot=(0.707107,0.707107,0;3.76991rad)
  shape: bbox 10.04 x 12.71 x 6.004 mm, 12 faces, 2 solids (baked)
FEATURE [Part::Feature] Fusion103077013004017008007
  Placement = pos=(7.06123,-7.06123,13.7447) rot=(-0.707107,-0.707107,0;1.88496rad)
  shape: bbox 11.79 x 12.81 x 4.715 mm, 12 faces, 2 solids (baked)
FEATURE [Part::Feature] Fusion103077013004017008008
  Placement = pos=(7.06123,-7.06123,7.25532) rot=(-0.707107,-0.707107,0;1.25664rad)
  shape: bbox 12.81 x 11.79 x 4.715 mm, 12 faces, 2 solids (baked)
FEATURE [Part::Feature] Fusion103077013004017008009
  Placement = pos=(4.36408,-4.36408,2.00532) rot=(-0.707107,-0.707107,0;0.628319rad)
  shape: bbox 12.71 x 10.04 x 6.004 mm, 12 faces, 2 solids (baked)
FEATURE [Part::MultiFuse] Fusion103077013004017008010
  Shapes = -> [Fusion103077013004017008001,Fusion103077013004017008003,Fusion103077013004017008007,Fusion103077013004017008005,Fusion103077013004017008009,Fusion103077013004017008008,Fusion103077013004017008004,Fusion103077013004017008002,Fusion103077013004017008,Fusion103077013004017008006]
FEATURE [Part::Cut] Cut173011019  label="Gear with Smaller Teeth 0.2"
  Base = -> Cut173011005
  Tool = -> Fusion103077013004017008010
note: 2 file-system paths scrubbed to <path> (originals preserved in the JSON sidecar)
